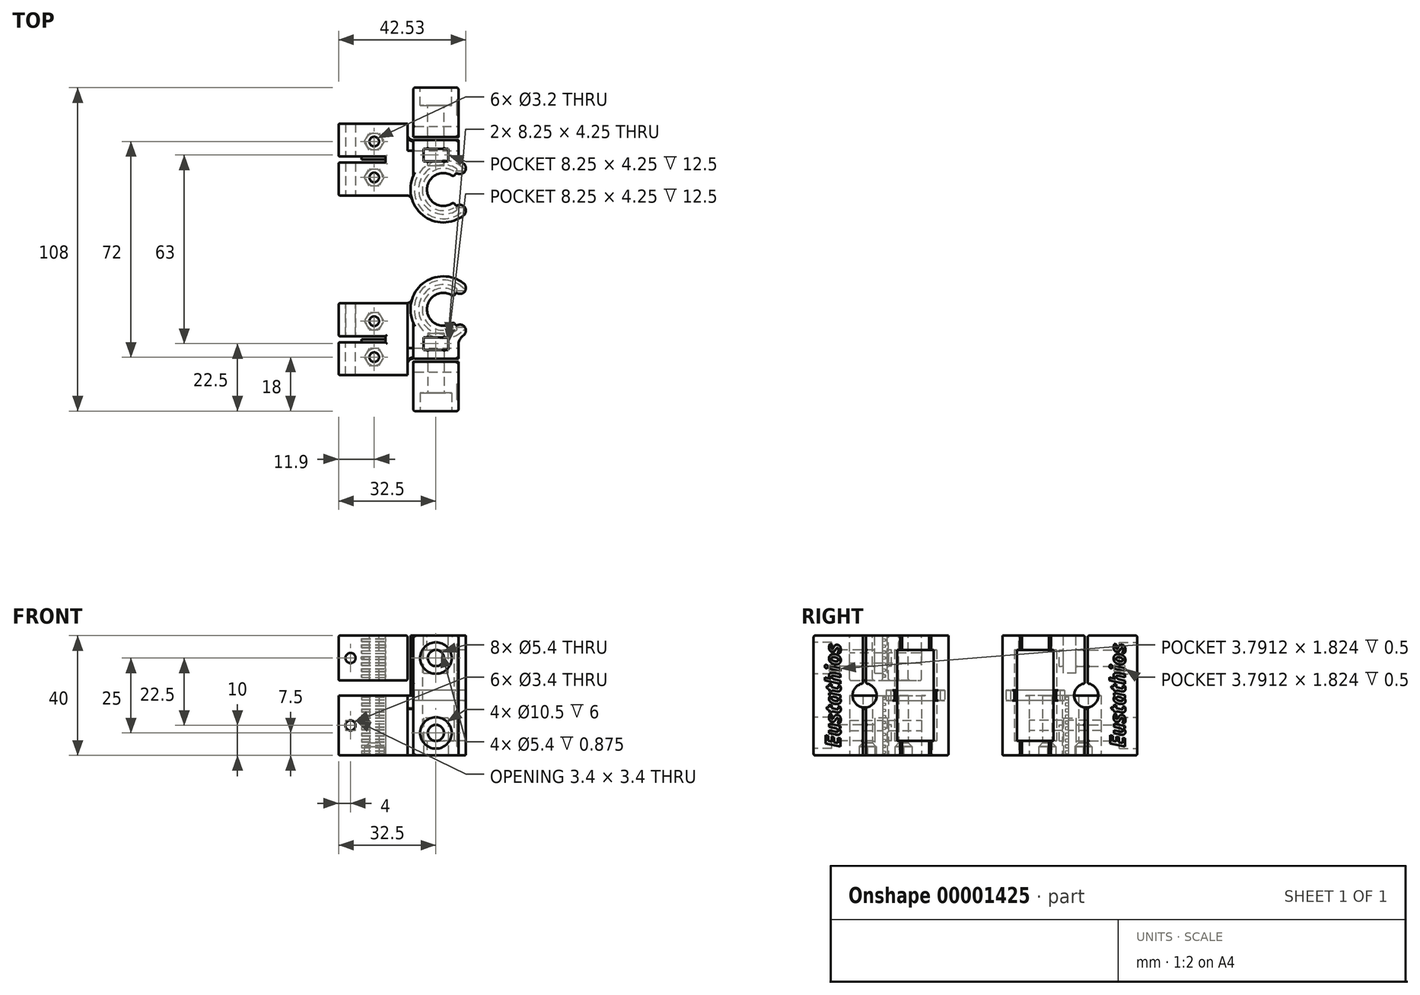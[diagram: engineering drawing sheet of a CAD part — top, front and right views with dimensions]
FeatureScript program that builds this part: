
annotation { "Feature Type Name" : "Feature", "Feature Type Description" : "" }
export const myFeature = defineFeature(function(context is Context, id is Id, definition is map)
    precondition{}
    {
        {
            var Q0;
            Q0=qCreatedBy(makeId("Top.planeOp"),FACE);
            var sketch = newSketch(context, id + "F0", { "sketchPlane" : qUnion([Q0])});
            skArc(sketch, "E0", {"start": v(5, -9.8) * mm, "mid": v(3.61, 10.39) * mm, "end": v(-10, -4.58) * mm});
            skLineSegment(sketch, "E1", {"start": v(5, -34) * mm, "end": v(5, -9.8) * mm});
            skLineSegment(sketch, "E2", {"start": v(-10, -4.58) * mm, "end": v(-10, -34) * mm});
            skLineSegment(sketch, "E3", {"start": v(-10, -34) * mm, "end": v(5, -34) * mm});
            skLineSegment(sketch, "E4", {"start": v(-10, -17) * mm, "end": v(5, -17) * mm, "construction": true});
            skSolve(sketch);
        }
        {
            var Q0;
            Q0=qSketchRegion(id+"F0",true);
            extrude(context, id + "F1", {"entities" : qUnion([Q0]), "depth" : 40 * mm});
        }
        {
            var Q0;
            Q0=makeQuery(id+"F1.opExtrude","CAP_FACE",FACE,{"disambiguationData":[OSD([sQuery(id+"F0.wireOp",EDGE,"E0"),sQuery(id+"F0.wireOp",EDGE,"E1"),sQuery(id+"F0.wireOp",EDGE,"E2"),sQuery(id+"F0.wireOp",EDGE,"E3")])],"isStart":true});
            var Q1;
            Q1=makeQuery(id+"F1.opExtrude","CAP_FACE",FACE,{"disambiguationData":[OSD([sQuery(id+"F0.wireOp",EDGE,"E0"),sQuery(id+"F0.wireOp",EDGE,"E1"),sQuery(id+"F0.wireOp",EDGE,"E2"),sQuery(id+"F0.wireOp",EDGE,"E3")])],"isStart":false});
            cPlane(context, id + "F2", {"entities" : qUnion([Q0, Q1]), "cplaneType" : CPlaneType.MID_PLANE, "offset" : 150 * mm, "width" : 150 * mm, "height" : 150 * mm});
        }
        {
            var Q0;
            Q0=makeQuery(id+"F1.opExtrude","CAP_FACE",FACE,{"disambiguationData":[OSD([sQuery(id+"F0.wireOp",EDGE,"E0"),sQuery(id+"F0.wireOp",EDGE,"E1"),sQuery(id+"F0.wireOp",EDGE,"E2"),sQuery(id+"F0.wireOp",EDGE,"E3")])],"isStart":true});
            var sketch = newSketch(context, id + "F3", { "sketchPlane" : qUnion([Q0])});
            skLineSegment(sketch, "E5", {"start": v(-35, -2) * mm, "end": v(-35, 9) * mm});
            skLineSegment(sketch, "E6", {"start": v(-35, 9) * mm, "end": v(-19.3, 9) * mm});
            skLineSegment(sketch, "E7", {"start": v(-19.3, 9) * mm, "end": v(-19.3, 11) * mm});
            skLineSegment(sketch, "E8", {"start": v(-19.3, 11) * mm, "end": v(-35, 11) * mm});
            skLineSegment(sketch, "E9", {"start": v(-35, 11) * mm, "end": v(-35, 22) * mm});
            skLineSegment(sketch, "E10", {"start": v(-35, 22) * mm, "end": v(-10, 22) * mm});
            skLineSegment(sketch, "E11", {"start": v(-10, 22) * mm, "end": v(-10, 4.58) * mm});
            skLineSegment(sketch, "E12", {"start": v(-35, 11) * mm, "end": v(-35, 9) * mm, "construction": true});
            skLineSegment(sketch, "E13", {"start": v(-35, 10) * mm, "end": v(-19.3, 10) * mm, "construction": true});
            skLineSegment(sketch, "E14", {"start": v(-35, -2) * mm, "end": v(-12.37, -2) * mm});
            skArc(sketch, "E15.0", {"start": v(-10.47, -3.38) * mm, "mid": v(-10.98, 0.64) * mm, "end": v(-10, 4.58) * mm});
            skArc(sketch, "E16", {"start": v(-12.37, -2) * mm, "mid": v(-11.2, -2.38) * mm, "end": v(-10.47, -3.38) * mm});
            skPoint(sketch, "E17.orphan", {"position": v(5, 9.8) * mm});
            skSolve(sketch);
        }
        {
            var Q0;
            Q0=qSketchRegion(id+"F3",true);
            var Q1;
            Q1=qCreatedBy(id+"F2.planeOp",FACE);
            extrude(context, id + "F4", {"entities" : qUnion([Q0]), "operationType" : NewBodyOperationType.ADD, "endBound" : BoundingType.UP_TO_SURFACE, "oppositeDirection" : true, "endBoundEntityFace" : qUnion([Q1]), "depth" : 21 * mm});
        }
        {
            var Q0;
            Q0=makeQuery(id+"F1.opExtrude","SWEPT_FACE",FACE,{"disambiguationData":[OSD([sQuery(id+"F0.wireOp",EDGE,"E1")])]});
            var sketch = newSketch(context, id + "F5", { "sketchPlane" : qUnion([Q0])});
            skLineSegment(sketch, "E18", {"start": v(0, 0) * mm, "end": v(0, 40) * mm, "construction": true});
            skLineSegment(sketch, "E19.0", {"start": v(-9.8, 40) * mm, "end": v(11, 40) * mm, "construction": true});
            skLineSegment(sketch, "E20", {"start": v(0, 20) * mm, "end": v(-17, 20) * mm, "construction": true});
            skPoint(sketch, "E20.endSnap0", {"position": v(0, 20) * mm});
            skLineSegment(sketch, "E21", {"start": v(-17, 20) * mm, "end": v(-34, 20) * mm, "construction": true});
            skCircle(sketch, "E22", {"center": v(-17, 20) * mm, "radius": 4.03 * mm});
            skSolve(sketch);
        }
        {
            var Q0;
            Q0=qSketchRegion(id+"F5",true);
            var Q1;
            Q1=makeQuery(id+"F1.opExtrude","SWEPT_FACE",FACE,{"disambiguationData":[OSD([sQuery(id+"F0.wireOp",EDGE,"E2")])]});
            extrude(context, id + "F6", {"entities" : qUnion([Q0]), "operationType" : NewBodyOperationType.REMOVE, "oppositeDirection" : true, "endBoundEntityFace" : qUnion([Q1]), "depth" : 17 * mm});
        }
        {
            var Q0;
            Q0=makeQuery(id+"F4.boolean.opBoolean","MERGE",FACE,{"derivedFrom":[makeQuery(id+"F1.opExtrude","CAP_FACE",FACE,{"disambiguationData":[OSD([sQuery(id+"F0.wireOp",EDGE,"E0"),sQuery(id+"F0.wireOp",EDGE,"E1"),sQuery(id+"F0.wireOp",EDGE,"E2"),sQuery(id+"F0.wireOp",EDGE,"E3")])],"isStart":true}),makeQuery(id+"F4.opExtrude","CAP_FACE",FACE,{"disambiguationData":[OSD([sQuery(id+"F3.wireOp",EDGE,"E5"),sQuery(id+"F3.wireOp",EDGE,"E6"),sQuery(id+"F3.wireOp",EDGE,"E7"),sQuery(id+"F3.wireOp",EDGE,"E8"),sQuery(id+"F3.wireOp",EDGE,"E9"),sQuery(id+"F3.wireOp",EDGE,"E10"),sQuery(id+"F3.wireOp",EDGE,"E11"),sQuery(id+"F3.wireOp",EDGE,"bca63a35-03c2-4865-813d-011e51dad5aa"),sQuery(id+"F3.wireOp",EDGE,"E14"),sQuery(id+"F3.wireOp",EDGE,"5d72e0aa-44b3-420c-8565-5770b2da08a5")])],"isStart":true})]});
            var sketch = newSketch(context, id + "F7", { "sketchPlane" : qUnion([Q0])});
            skLineSegment(sketch, "E23.0", {"start": v(-12, 12.98) * mm, "end": v(-10, 12.98) * mm, "construction": true});
            skLineSegment(sketch, "E24.0", {"start": v(-12, 12.97) * mm, "end": v(-12, 12.97) * mm});
            skLineSegment(sketch, "E25", {"start": v(-10, 17.5) * mm, "end": v(5, 17.5) * mm});
            skLineSegment(sketch, "E26", {"start": v(5, 17.5) * mm, "end": v(5, 16.5) * mm});
            skLineSegment(sketch, "E27", {"start": v(5, 17) * mm, "end": v(-12, 17) * mm, "construction": true});
            skLineSegment(sketch, "E28", {"start": v(5, 16.5) * mm, "end": v(-10, 16.5) * mm});
            skLineSegment(sketch, "E29.0", {"start": v(-12, 12.97) * mm, "end": v(-12, 21.03) * mm, "construction": true});
            skLineSegment(sketch, "E30", {"start": v(-10, 22) * mm, "end": v(-10, 17.5) * mm});
            skLineSegment(sketch, "E31", {"start": v(-10, 22) * mm, "end": v(-12, 22) * mm});
            skLineSegment(sketch, "E32", {"start": v(-12, 22) * mm, "end": v(-12, 18.5) * mm});
            skPoint(sketch, "E33.visualSharp", {"position": v(-12, 16.5) * mm});
            skArc(sketch, "E33.filletArc", {"start": v(-12, 18.5) * mm, "mid": v(-11.41, 17.09) * mm, "end": v(-10, 16.5) * mm});
            skSolve(sketch);
        }
        {
            var Q0;
            Q0=qSketchRegion(id+"F7",true);
            extrude(context, id + "F8", {"entities" : qUnion([Q0]), "operationType" : NewBodyOperationType.REMOVE, "endBound" : BoundingType.THROUGH_ALL, "oppositeDirection" : true, "depth" : 25 * mm});
        }
        {
            var Q0;
            {var subQ0=sQuery(id+"F3.wireOp",EDGE,"E10");var subQ1=sQuery(id+"F3.wireOp",EDGE,"E9");var subQ2=sQuery(id+"F3.wireOp",EDGE,"E8");var subQ3=sQuery(id+"F3.wireOp",EDGE,"E7");var subQ4=sQuery(id+"F0.wireOp",EDGE,"E1");var subQ5=sQuery(id+"F0.wireOp",EDGE,"E0");var subQ6=sQuery(id+"F3.wireOp",EDGE,"5d72e0aa-44b3-420c-8565-5770b2da08a5");var subQ7=sQuery(id+"F3.wireOp",EDGE,"E14");var subQ8=sQuery(id+"F3.wireOp",EDGE,"E5");var subQ9=sQuery(id+"F3.wireOp",EDGE,"E6");Q0=makeQuery(id+"F8.boolean.opBoolean","SPLIT",FACE,{"disambiguationData":[TD([makeQuery(id+"F1.opExtrude","SWEPT_FACE",FACE,{"disambiguationData":[OSD([subQ5])]})])],"derivedFrom":makeQuery(id+"F4.boolean.opBoolean","MERGE",FACE,{"derivedFrom":[makeQuery(id+"F1.opExtrude","CAP_FACE",FACE,{"disambiguationData":[OSD([subQ5,subQ4,sQuery(id+"F0.wireOp",EDGE,"E2"),sQuery(id+"F0.wireOp",EDGE,"E3")])],"isStart":true}),makeQuery(id+"F4.opExtrude","CAP_FACE",FACE,{"disambiguationData":[OSD([subQ8,subQ9,subQ3,subQ2,subQ1,subQ0,sQuery(id+"F3.wireOp",EDGE,"E11"),sQuery(id+"F3.wireOp",EDGE,"bca63a35-03c2-4865-813d-011e51dad5aa"),subQ7,subQ6])],"isStart":true})]})});}
            var sketch = newSketch(context, id + "F9", { "sketchPlane" : qUnion([Q0])});
            skCircle(sketch, "E34", {"center": v(0, 0) * mm, "radius": 7.05 * mm});
            skSolve(sketch);
        }
        {
            var Q0;
            Q0=qSketchRegion(id+"F9",true);
            extrude(context, id + "F10", {"entities" : qUnion([Q0]), "operationType" : NewBodyOperationType.REMOVE, "endBound" : BoundingType.THROUGH_ALL, "oppositeDirection" : true, "depth" : 25 * mm});
        }
        {
            var Q0;
            {var subQ0=sQuery(id+"F3.wireOp",EDGE,"E10");var subQ1=sQuery(id+"F3.wireOp",EDGE,"E9");var subQ2=sQuery(id+"F3.wireOp",EDGE,"E8");var subQ3=sQuery(id+"F3.wireOp",EDGE,"E7");var subQ4=sQuery(id+"F0.wireOp",EDGE,"E1");var subQ5=sQuery(id+"F0.wireOp",EDGE,"E0");var subQ6=sQuery(id+"F3.wireOp",EDGE,"5d72e0aa-44b3-420c-8565-5770b2da08a5");var subQ7=sQuery(id+"F3.wireOp",EDGE,"E14");var subQ8=sQuery(id+"F3.wireOp",EDGE,"E5");var subQ9=sQuery(id+"F3.wireOp",EDGE,"E6");Q0=makeQuery(id+"F8.boolean.opBoolean","SPLIT",FACE,{"disambiguationData":[TD([makeQuery(id+"F1.opExtrude","SWEPT_FACE",FACE,{"disambiguationData":[OSD([subQ5])]})])],"derivedFrom":makeQuery(id+"F4.boolean.opBoolean","MERGE",FACE,{"derivedFrom":[makeQuery(id+"F1.opExtrude","CAP_FACE",FACE,{"disambiguationData":[OSD([subQ5,subQ4,sQuery(id+"F0.wireOp",EDGE,"E2"),sQuery(id+"F0.wireOp",EDGE,"E3")])],"isStart":true}),makeQuery(id+"F4.opExtrude","CAP_FACE",FACE,{"disambiguationData":[OSD([subQ8,subQ9,subQ3,subQ2,subQ1,subQ0,sQuery(id+"F3.wireOp",EDGE,"E11"),sQuery(id+"F3.wireOp",EDGE,"bca63a35-03c2-4865-813d-011e51dad5aa"),subQ7,subQ6])],"isStart":true})]})});}
            var sketch = newSketch(context, id + "F11", { "sketchPlane" : qUnion([Q0])});
            skLineSegment(sketch, "E35", {"start": v(0, 0) * mm, "end": v(8.5, 6.98) * mm, "construction": true});
            skLineSegment(sketch, "E36", {"start": v(8.5, -6.98) * mm, "end": v(0, 0) * mm, "construction": true});
            skArc(sketch, "E37", {"start": v(6.77, -8.67) * mm, "mid": v(7.11, -5.9) * mm, "end": v(4.34, -5.56) * mm});
            skLineSegment(sketch, "E38", {"start": v(0, 0) * mm, "end": v(14.65, 0) * mm, "construction": true});
            skArc(sketch, "E39", {"start": v(4.34, 5.56) * mm, "mid": v(7.11, 5.9) * mm, "end": v(6.77, 8.67) * mm});
            skLineSegment(sketch, "E40", {"start": v(5.56, 7.11) * mm, "end": v(0, 0) * mm, "construction": true});
            skLineSegment(sketch, "E41", {"start": v(0, 0) * mm, "end": v(5.56, -7.11) * mm, "construction": true});
            skArc(sketch, "E42", {"start": v(4.34, 5.56) * mm, "mid": v(7.05, 0) * mm, "end": v(4.34, -5.56) * mm});
            skSolve(sketch);
        }
        {
            var Q0;
            Q0=qSketchRegion(id+"F11",true);
            var Q1;
            {var subQ2=sQuery(id+"F11.wireOp",EDGE,"E37");Q1=makeQuery(id+"F11.imprint","IMPRINT",FACE,{"disambiguationData":[TD([[makeQuery(id+"F11.imprint","IMPRINT",EDGE,{"derivedFrom":subQ2}),-1.0]])]});}
            extrude(context, id + "F12", {"entities" : qUnion([Q0, Q1]), "operationType" : NewBodyOperationType.REMOVE, "endBound" : BoundingType.THROUGH_ALL, "oppositeDirection" : true, "depth" : 25 * mm});
        }
        {
            var Q0;
            Q0=makeQuery(id+"F1.opExtrude","SWEPT_EDGE",EDGE,{"disambiguationData":[OSD([sQuery(id+"F0.wireOp",EDGE,"E0"),sQuery(id+"F0.wireOp",EDGE,"E1")])]});
            fillet(context, id + "F13", {"entities" : qUnion([Q0]), "radius" : 4 * mm, "tangentPropagation" : true, "allowEdgeOverflow" : false});
        }
        {
            var Q0;
            Q0=qCreatedBy(makeId("Right.planeOp"),FACE);
            var sketch = newSketch(context, id + "F14", { "sketchPlane" : qUnion([Q0])});
            skLineSegment(sketch, "E43.rect.bottom", {"start": v(-6.1, 35.2) * mm, "end": v(6.1, 35.2) * mm});
            skLineSegment(sketch, "E43.rect.top", {"start": v(-6.1, 4.8) * mm, "end": v(6.1, 4.8) * mm});
            skLineSegment(sketch, "E43.rect.left", {"start": v(-6.1, 35.2) * mm, "end": v(-6.1, 4.8) * mm});
            skLineSegment(sketch, "E43.rect.right", {"start": v(6.1, 35.2) * mm, "end": v(6.1, 4.8) * mm});
            skPoint(sketch, "E43.rect.middle", {"position": v(0, 20) * mm});
            skLineSegment(sketch, "E44", {"start": v(-5.14, 40) * mm, "end": v(-5.14, 0) * mm, "construction": true});
            skLineSegment(sketch, "E45", {"start": v(5.14, 0) * mm, "end": v(5.14, 40) * mm, "construction": true});
            skLineSegment(sketch, "E46", {"start": v(-5.14, 0) * mm, "end": v(5.14, 0) * mm, "construction": true});
            skLineSegment(sketch, "E47", {"start": v(-5.14, 40) * mm, "end": v(5.14, 40) * mm, "construction": true});
            skLineSegment(sketch, "E48", {"start": v(0, 0) * mm, "end": v(0, 40) * mm, "construction": true});
            skSolve(sketch);
        }
        {
            var Q0;
            Q0=qSketchRegion(id+"F14",true);
            extrude(context, id + "F15", {"entities" : qUnion([Q0]), "operationType" : NewBodyOperationType.REMOVE, "endBound" : BoundingType.THROUGH_ALL, "depth" : 25 * mm});
        }
        {
            var Q0;
            {var subQ0=sQuery(id+"F3.wireOp",EDGE,"E10");var subQ1=sQuery(id+"F3.wireOp",EDGE,"E9");var subQ2=sQuery(id+"F3.wireOp",EDGE,"E8");var subQ3=sQuery(id+"F3.wireOp",EDGE,"E7");var subQ4=sQuery(id+"F0.wireOp",EDGE,"E1");var subQ5=sQuery(id+"F0.wireOp",EDGE,"E0");var subQ6=sQuery(id+"F3.wireOp",EDGE,"5d72e0aa-44b3-420c-8565-5770b2da08a5");var subQ7=sQuery(id+"F3.wireOp",EDGE,"E14");var subQ8=sQuery(id+"F3.wireOp",EDGE,"E5");var subQ9=sQuery(id+"F3.wireOp",EDGE,"E6");Q0=makeQuery(id+"F8.boolean.opBoolean","SPLIT",FACE,{"disambiguationData":[TD([makeQuery(id+"F1.opExtrude","SWEPT_FACE",FACE,{"disambiguationData":[OSD([subQ5])]})])],"derivedFrom":makeQuery(id+"F4.boolean.opBoolean","MERGE",FACE,{"derivedFrom":[makeQuery(id+"F1.opExtrude","CAP_FACE",FACE,{"disambiguationData":[OSD([subQ5,subQ4,sQuery(id+"F0.wireOp",EDGE,"E2"),sQuery(id+"F0.wireOp",EDGE,"E3")])],"isStart":true}),makeQuery(id+"F4.opExtrude","CAP_FACE",FACE,{"disambiguationData":[OSD([subQ8,subQ9,subQ3,subQ2,subQ1,subQ0,sQuery(id+"F3.wireOp",EDGE,"E11"),sQuery(id+"F3.wireOp",EDGE,"bca63a35-03c2-4865-813d-011e51dad5aa"),subQ7,subQ6])],"isStart":true})]})});}
            var sketch = newSketch(context, id + "F16", { "sketchPlane" : qUnion([Q0])});
            skArc(sketch, "E49", {"start": v(3.39, 4.33) * mm, "mid": v(-5.5, 0) * mm, "end": v(3.39, -4.33) * mm});
            skArc(sketch, "E50.0", {"start": v(4.34, 5.56) * mm, "mid": v(-7.05, 0) * mm, "end": v(4.34, -5.56) * mm});
            skLineSegment(sketch, "E51", {"start": v(0, 0) * mm, "end": v(6.8, 5.58) * mm, "construction": true});
            skLineSegment(sketch, "E52", {"start": v(0, 0) * mm, "end": v(6.8, -5.58) * mm, "construction": true});
            skArc(sketch, "E53", {"start": v(4.34, 5.56) * mm, "mid": v(5.58, 5.14) * mm, "end": v(6.8, 5.58) * mm});
            skArc(sketch, "E54", {"start": v(4.34, -5.56) * mm, "mid": v(5.58, -5.14) * mm, "end": v(6.8, -5.58) * mm});
            skLineSegment(sketch, "E55", {"start": v(4.34, 5.56) * mm, "end": v(3.39, 4.33) * mm});
            skLineSegment(sketch, "E56", {"start": v(3.39, -4.33) * mm, "end": v(4.34, -5.56) * mm});
            skLineSegment(sketch, "E57", {"start": v(3.39, 4.33) * mm, "end": v(0, 0) * mm, "construction": true});
            skLineSegment(sketch, "E58", {"start": v(3.39, -4.33) * mm, "end": v(0, 0) * mm, "construction": true});
            skSolve(sketch);
        }
        {
            var Q0;
            Q0=qSketchRegion(id+"F16",true);
            var Q1;
            Q1=makeQuery(id+"F15.boolean.opBoolean","COPY",FACE,{"disambiguationData":[OD(0.0)],"derivedFrom":makeQuery(id+"F15.opExtrude","SWEPT_FACE",FACE,{"disambiguationData":[OSD([sQuery(id+"F14.wireOp",EDGE,"E43.rect.top")])]})});
            extrude(context, id + "F17", {"entities" : qUnion([Q0]), "operationType" : NewBodyOperationType.ADD, "endBound" : BoundingType.UP_TO_SURFACE, "oppositeDirection" : true, "endBoundEntityFace" : qUnion([Q1]), "depth" : 2.4 * mm});
        }
        {
            var Q0;
            {var subQ0=sQuery(id+"F0.wireOp",EDGE,"E0");var subQ1=sQuery(id+"F0.wireOp",EDGE,"E1");var subQ2=sQuery(id+"F0.wireOp",EDGE,"E2");Q0=makeQuery(id+"F8.boolean.opBoolean","SPLIT",FACE,{"disambiguationData":[TD([makeQuery(id+"F1.opExtrude","SWEPT_FACE",FACE,{"disambiguationData":[OSD([subQ0])]})])],"derivedFrom":makeQuery(id+"F1.opExtrude","CAP_FACE",FACE,{"disambiguationData":[OSD([subQ0,subQ1,subQ2,sQuery(id+"F0.wireOp",EDGE,"E3")])],"isStart":false})});}
            var sketch = newSketch(context, id + "F18", { "sketchPlane" : qUnion([Q0])});
            skArc(sketch, "E59.0", {"start": v(3.39, -4.33) * mm, "mid": v(-5.5, 0) * mm, "end": v(3.39, 4.33) * mm});
            skLineSegment(sketch, "E60.0", {"start": v(4.34, -5.56) * mm, "end": v(3.39, -4.33) * mm});
            skLineSegment(sketch, "E61.0", {"start": v(3.39, 4.33) * mm, "end": v(4.34, 5.56) * mm});
            skArc(sketch, "E62.0", {"start": v(4.34, 5.56) * mm, "mid": v(-7.05, 0) * mm, "end": v(4.34, -5.56) * mm});
            skSolve(sketch);
        }
        {
            var Q0;
            Q0=qSketchRegion(id+"F18",true);
            var Q1;
            Q1=makeQuery(id+"F15.boolean.opBoolean","COPY",FACE,{"disambiguationData":[OD(0.0)],"derivedFrom":makeQuery(id+"F15.opExtrude","SWEPT_FACE",FACE,{"disambiguationData":[OSD([sQuery(id+"F14.wireOp",EDGE,"E43.rect.bottom")])]})});
            extrude(context, id + "F19", {"entities" : qUnion([Q0]), "operationType" : NewBodyOperationType.ADD, "endBound" : BoundingType.UP_TO_SURFACE, "oppositeDirection" : true, "endBoundEntityFace" : qUnion([Q1]), "depth" : 2.4 * mm});
        }
        {
            var Q0;
            {var subQ0=sQuery(id+"F0.wireOp",EDGE,"E0");var subQ1=sQuery(id+"F0.wireOp",EDGE,"E1");var subQ2=sQuery(id+"F0.wireOp",EDGE,"E2");Q0=makeQuery(id+"F19.boolean.opBoolean","MERGE",FACE,{"derivedFrom":[makeQuery(id+"F8.boolean.opBoolean","SPLIT",FACE,{"disambiguationData":[TD([makeQuery(id+"F1.opExtrude","SWEPT_FACE",FACE,{"disambiguationData":[OSD([subQ0])]})])],"derivedFrom":makeQuery(id+"F1.opExtrude","CAP_FACE",FACE,{"disambiguationData":[OSD([subQ0,subQ1,subQ2,sQuery(id+"F0.wireOp",EDGE,"E3")])],"isStart":false})}),makeQuery(id+"F19.opExtrude","CAP_FACE",FACE,{"disambiguationData":[OSD([sQuery(id+"F18.wireOp",EDGE,"825981b6-10bd-436c-b23c-b1dcfb23399f.0"),sQuery(id+"F18.wireOp",EDGE,"26848335-8289-480a-91f7-f3094b967ab5.0"),sQuery(id+"F18.wireOp",EDGE,"958e6e3c-ce8c-4eca-b8df-495d4845233b.0"),sQuery(id+"F18.wireOp",EDGE,"a21f0ce2-bef5-4404-b2f3-7f19712db0ed.0"),sQuery(id+"F18.wireOp",EDGE,"5b232a10-1d2d-4218-a2a3-206db68530f9.0"),sQuery(id+"F18.wireOp",EDGE,"9355f6d4-eb2a-417f-8d43-74a68f565168.0")])],"isStart":true})]});}
            var sketch = newSketch(context, id + "F20", { "sketchPlane" : qUnion([Q0])});
            skLineSegment(sketch, "E63", {"start": v(-2.5, -16.5) * mm, "end": v(-2.5, -11.5) * mm, "construction": true});
            skLineSegment(sketch, "E64.rect.bottom", {"start": v(-6.62, -13.62) * mm, "end": v(1.63, -13.62) * mm});
            skLineSegment(sketch, "E64.rect.top", {"start": v(-6.62, -9.38) * mm, "end": v(1.63, -9.38) * mm});
            skLineSegment(sketch, "E64.rect.left", {"start": v(-6.62, -13.62) * mm, "end": v(-6.62, -9.38) * mm});
            skLineSegment(sketch, "E64.rect.right", {"start": v(1.63, -13.63) * mm, "end": v(1.63, -9.38) * mm});
            skPoint(sketch, "E64.rect.middle", {"position": v(-2.5, -11.5) * mm});
            skSolve(sketch);
        }
        {
            var Q0;
            Q0=qSketchRegion(id+"F20",true);
            extrude(context, id + "F21", {"entities" : qUnion([Q0]), "operationType" : NewBodyOperationType.REMOVE, "oppositeDirection" : true, "depth" : 12.5 * mm});
        }
        {
            var Q0;
            {var subQ0=sQuery(id+"F3.wireOp",EDGE,"E10");var subQ1=sQuery(id+"F3.wireOp",EDGE,"E9");var subQ2=sQuery(id+"F3.wireOp",EDGE,"E8");var subQ3=sQuery(id+"F3.wireOp",EDGE,"E7");var subQ4=sQuery(id+"F0.wireOp",EDGE,"E1");var subQ5=sQuery(id+"F0.wireOp",EDGE,"E0");var subQ6=sQuery(id+"F3.wireOp",EDGE,"5d72e0aa-44b3-420c-8565-5770b2da08a5");var subQ7=sQuery(id+"F3.wireOp",EDGE,"E14");var subQ8=sQuery(id+"F3.wireOp",EDGE,"E5");var subQ9=sQuery(id+"F3.wireOp",EDGE,"E6");Q0=makeQuery(id+"F17.boolean.opBoolean","MERGE",FACE,{"derivedFrom":[makeQuery(id+"F8.boolean.opBoolean","SPLIT",FACE,{"disambiguationData":[TD([makeQuery(id+"F1.opExtrude","SWEPT_FACE",FACE,{"disambiguationData":[OSD([subQ5])]})])],"derivedFrom":makeQuery(id+"F4.boolean.opBoolean","MERGE",FACE,{"derivedFrom":[makeQuery(id+"F1.opExtrude","CAP_FACE",FACE,{"disambiguationData":[OSD([subQ5,subQ4,sQuery(id+"F0.wireOp",EDGE,"E2"),sQuery(id+"F0.wireOp",EDGE,"E3")])],"isStart":true}),makeQuery(id+"F4.opExtrude","CAP_FACE",FACE,{"disambiguationData":[OSD([subQ8,subQ9,subQ3,subQ2,subQ1,subQ0,sQuery(id+"F3.wireOp",EDGE,"E11"),sQuery(id+"F3.wireOp",EDGE,"bca63a35-03c2-4865-813d-011e51dad5aa"),subQ7,subQ6])],"isStart":true})]})}),makeQuery(id+"F17.opExtrude","CAP_FACE",FACE,{"disambiguationData":[OSD([sQuery(id+"F16.wireOp",EDGE,"E49"),sQuery(id+"F16.wireOp",EDGE,"E50.0"),sQuery(id+"F16.wireOp",EDGE,"E55"),sQuery(id+"F16.wireOp",EDGE,"E56")])],"isStart":true})]});}
            var sketch = newSketch(context, id + "F22", { "sketchPlane" : qUnion([Q0])});
            skLineSegment(sketch, "E65.0.0", {"start": v(-6.62, 9.38) * mm, "end": v(-6.62, 13.62) * mm});
            skLineSegment(sketch, "E65.0.1", {"start": v(-6.62, 13.62) * mm, "end": v(1.63, 13.62) * mm});
            skLineSegment(sketch, "E65.0.2", {"start": v(1.63, 13.62) * mm, "end": v(1.63, 9.38) * mm});
            skLineSegment(sketch, "E65.0.3", {"start": v(1.63, 9.38) * mm, "end": v(-6.62, 9.38) * mm});
            skSolve(sketch);
        }
        {
            var Q0;
            Q0=qSketchRegion(id+"F22",true);
            extrude(context, id + "F23", {"entities" : qUnion([Q0]), "operationType" : NewBodyOperationType.REMOVE, "oppositeDirection" : true, "depth" : 12.5 * mm});
        }
        {
            var Q0;
            Q0=makeQuery(id+"F1.opExtrude","SWEPT_FACE",FACE,{"disambiguationData":[OSD([sQuery(id+"F0.wireOp",EDGE,"E3")])]});
            var sketch = newSketch(context, id + "F24", { "sketchPlane" : qUnion([Q0])});
            skLineSegment(sketch, "E66", {"start": v(-2.5, 0) * mm, "end": v(-2.5, 7.5) * mm, "construction": true});
            skLineSegment(sketch, "E67", {"start": v(-2.5, 7.5) * mm, "end": v(-2.5, 32.5) * mm, "construction": true});
            skLineSegment(sketch, "E68", {"start": v(-2.5, 32.5) * mm, "end": v(-2.5, 40) * mm, "construction": true});
            skLineSegment(sketch, "E69", {"start": v(-2.5, 7.5) * mm, "end": v(-10, 7.5) * mm, "construction": true});
            skLineSegment(sketch, "E70", {"start": v(-2.5, 32.5) * mm, "end": v(-10, 32.5) * mm, "construction": true});
            skCircle(sketch, "E71", {"center": v(-2.5, 7.5) * mm, "radius": 2.7 * mm});
            skCircle(sketch, "E72", {"center": v(-2.5, 32.5) * mm, "radius": 2.7 * mm});
            skSolve(sketch);
        }
        {
            var Q0;
            Q0=qSketchRegion(id+"F24",true);
            extrude(context, id + "F25", {"entities" : qUnion([Q0]), "operationType" : NewBodyOperationType.REMOVE, "oppositeDirection" : true, "depth" : 26 * mm, "offsetDistance" : 25 * mm});
        }
        {
            var Q0;
            Q0=makeQuery(id+"F1.opExtrude","SWEPT_FACE",FACE,{"disambiguationData":[OSD([sQuery(id+"F0.wireOp",EDGE,"E3")])]});
            var sketch = newSketch(context, id + "F26", { "sketchPlane" : qUnion([Q0])});
            skCircle(sketch, "E73", {"center": v(-2.5, 32.5) * mm, "radius": 5.25 * mm});
            skCircle(sketch, "E74", {"center": v(-2.5, 7.5) * mm, "radius": 5.25 * mm});
            skSolve(sketch);
        }
        {
            var Q0;
            Q0=qSketchRegion(id+"F26",true);
            extrude(context, id + "F27", {"entities" : qUnion([Q0]), "operationType" : NewBodyOperationType.REMOVE, "oppositeDirection" : true, "depth" : 6 * mm});
        }
        {
            var Q0;
            Q0=makeQuery(id+"F8.boolean.opBoolean","INTERSECT",EDGE,{"derivedFrom":[makeQuery(id+"F6.boolean.opBoolean","COPY",FACE,{"derivedFrom":makeQuery(id+"F6.opExtrude","SWEPT_FACE",FACE,{"disambiguationData":[OSD([sQuery(id+"F5.wireOp",EDGE,"E22")])]})}),makeQuery(id+"F8.opExtrude","SWEPT_FACE",FACE,{"disambiguationData":[OSD([sQuery(id+"F7.wireOp",EDGE,"E30")])]})]});
            var Q1;
            Q1=makeQuery(id+"F8.boolean.opBoolean","INTERSECT",EDGE,{"disambiguationData":[OD(0.0)],"derivedFrom":[makeQuery(id+"F6.boolean.opBoolean","COPY",FACE,{"derivedFrom":makeQuery(id+"F6.opExtrude","SWEPT_FACE",FACE,{"disambiguationData":[OSD([sQuery(id+"F5.wireOp",EDGE,"E22")])]})}),makeQuery(id+"F8.opExtrude","SWEPT_FACE",FACE,{"disambiguationData":[OSD([sQuery(id+"F7.wireOp",EDGE,"E25")])]})]});
            var Q2;
            Q2=makeQuery(id+"F8.boolean.opBoolean","INTERSECT",EDGE,{"disambiguationData":[OD(1.0)],"derivedFrom":[makeQuery(id+"F6.boolean.opBoolean","COPY",FACE,{"derivedFrom":makeQuery(id+"F6.opExtrude","SWEPT_FACE",FACE,{"disambiguationData":[OSD([sQuery(id+"F5.wireOp",EDGE,"E22")])]})}),makeQuery(id+"F8.opExtrude","SWEPT_FACE",FACE,{"disambiguationData":[OSD([sQuery(id+"F7.wireOp",EDGE,"E25")])]})]});
            var Q3;
            Q3=makeQuery(id+"F8.boolean.opBoolean","COPY",EDGE,{"disambiguationData":[OD(0.0)],"derivedFrom":makeQuery(id+"F8.opExtrude","SWEPT_EDGE",EDGE,{"disambiguationData":[OSD([sQuery(id+"F7.wireOp",EDGE,"E25"),sQuery(id+"F7.wireOp",EDGE,"E30")])]})});
            var Q4;
            Q4=makeQuery(id+"F8.boolean.opBoolean","COPY",EDGE,{"disambiguationData":[OD(1.0)],"derivedFrom":makeQuery(id+"F8.opExtrude","SWEPT_EDGE",EDGE,{"disambiguationData":[OSD([sQuery(id+"F7.wireOp",EDGE,"E25"),sQuery(id+"F7.wireOp",EDGE,"E30")])]})});
            var Q5;
            Q5=makeQuery(id+"F8.boolean.opBoolean","INTERSECT",EDGE,{"derivedFrom":[makeQuery(id+"F1.opExtrude","CAP_FACE",FACE,{"disambiguationData":[OSD([sQuery(id+"F0.wireOp",EDGE,"E0"),sQuery(id+"F0.wireOp",EDGE,"E1"),sQuery(id+"F0.wireOp",EDGE,"E2"),sQuery(id+"F0.wireOp",EDGE,"E3")])],"isStart":false}),makeQuery(id+"F8.opExtrude","SWEPT_FACE",FACE,{"disambiguationData":[OSD([sQuery(id+"F7.wireOp",EDGE,"E25")])]})]});
            var Q6;
            {var subQ0=sQuery(id+"F0.wireOp",EDGE,"E2");var subQ1=sQuery(id+"F0.wireOp",EDGE,"E3");Q6=makeQuery(id+"F8.boolean.opBoolean","SPLIT",EDGE,{"disambiguationData":[TD([makeQuery(id+"F1.opExtrude","SWEPT_FACE",FACE,{"disambiguationData":[OSD([subQ1])]})])],"derivedFrom":makeQuery(id+"F1.opExtrude","CAP_EDGE",EDGE,{"disambiguationData":[OSD([subQ0])],"isStart":false})});}
            var Q7;
            Q7=makeQuery(id+"F1.opExtrude","CAP_EDGE",EDGE,{"disambiguationData":[OSD([sQuery(id+"F0.wireOp",EDGE,"E3")])],"isStart":false});
            var Q8;
            {var subQ0=sQuery(id+"F0.wireOp",EDGE,"E1");var subQ1=sQuery(id+"F0.wireOp",EDGE,"E3");Q8=makeQuery(id+"F8.boolean.opBoolean","SPLIT",EDGE,{"disambiguationData":[TD([makeQuery(id+"F1.opExtrude","SWEPT_FACE",FACE,{"disambiguationData":[OSD([subQ1])]})])],"derivedFrom":makeQuery(id+"F1.opExtrude","CAP_EDGE",EDGE,{"disambiguationData":[OSD([subQ0])],"isStart":false})});}
            var Q9;
            Q9=makeQuery(id+"F1.opExtrude","SWEPT_EDGE",EDGE,{"disambiguationData":[OSD([sQuery(id+"F0.wireOp",EDGE,"E2"),sQuery(id+"F0.wireOp",EDGE,"E3")])]});
            var Q10;
            Q10=makeQuery(id+"F1.opExtrude","SWEPT_EDGE",EDGE,{"disambiguationData":[OSD([sQuery(id+"F0.wireOp",EDGE,"E1"),sQuery(id+"F0.wireOp",EDGE,"E3")])]});
            var Q11;
            Q11=makeQuery(id+"F1.opExtrude","CAP_EDGE",EDGE,{"disambiguationData":[OSD([sQuery(id+"F0.wireOp",EDGE,"E3")])],"isStart":true});
            var Q12;
            Q12=makeQuery(id+"F8.boolean.opBoolean","COPY",EDGE,{"disambiguationData":[OD(1.0)],"derivedFrom":makeQuery(id+"F8.opExtrude","SWEPT_EDGE",EDGE,{"disambiguationData":[OSD([sQuery(id+"F0.wireOp",EDGE,"E1"),sQuery(id+"F7.wireOp",EDGE,"E25"),sQuery(id+"F7.wireOp",EDGE,"E26")])]})});
            var Q13;
            Q13=makeQuery(id+"F8.boolean.opBoolean","INTERSECT",EDGE,{"disambiguationData":[OD(1.0)],"derivedFrom":[makeQuery(id+"F6.boolean.opBoolean","COPY",FACE,{"derivedFrom":makeQuery(id+"F6.opExtrude","SWEPT_FACE",FACE,{"disambiguationData":[OSD([sQuery(id+"F5.wireOp",EDGE,"E22")])]})}),makeQuery(id+"F8.opExtrude","SWEPT_FACE",FACE,{"disambiguationData":[OSD([sQuery(id+"F7.wireOp",EDGE,"E25")])]})]});
            var Q14;
            Q14=makeQuery(id+"F8.boolean.opBoolean","COPY",EDGE,{"disambiguationData":[OD(0.0)],"derivedFrom":makeQuery(id+"F8.opExtrude","SWEPT_EDGE",EDGE,{"disambiguationData":[OSD([sQuery(id+"F0.wireOp",EDGE,"E1"),sQuery(id+"F7.wireOp",EDGE,"E25"),sQuery(id+"F7.wireOp",EDGE,"E26")])]})});
            var Q15;
            Q15=makeQuery(id+"F8.boolean.opBoolean","COPY",EDGE,{"derivedFrom":makeQuery(id+"F8.opExtrude","CAP_EDGE",EDGE,{"disambiguationData":[OSD([sQuery(id+"F7.wireOp",EDGE,"E25")])],"isStart":true})});
            var Q16;
            {var subQ0=sQuery(id+"F0.wireOp",EDGE,"E1");var subQ1=sQuery(id+"F0.wireOp",EDGE,"E3");Q16=makeQuery(id+"F8.boolean.opBoolean","SPLIT",EDGE,{"disambiguationData":[TD([makeQuery(id+"F1.opExtrude","SWEPT_FACE",FACE,{"disambiguationData":[OSD([subQ1])]})])],"derivedFrom":makeQuery(id+"F1.opExtrude","CAP_EDGE",EDGE,{"disambiguationData":[OSD([subQ0])],"isStart":true})});}
            var Q17;
            Q17=makeQuery(id+"F8.boolean.opBoolean","MERGE",EDGE,{"derivedFrom":[makeQuery(id+"F1.opExtrude","CAP_EDGE",EDGE,{"disambiguationData":[OSD([sQuery(id+"F0.wireOp",EDGE,"E2")])],"isStart":true}),makeQuery(id+"F8.opExtrude","CAP_EDGE",EDGE,{"disambiguationData":[OSD([sQuery(id+"F7.wireOp",EDGE,"E30")])],"isStart":true})]});
            var Q18;
            Q18=makeQuery(id+"F8.boolean.opBoolean","INTERSECT",EDGE,{"disambiguationData":[OD(0.0)],"derivedFrom":[makeQuery(id+"F6.boolean.opBoolean","COPY",FACE,{"derivedFrom":makeQuery(id+"F6.opExtrude","SWEPT_FACE",FACE,{"disambiguationData":[OSD([sQuery(id+"F5.wireOp",EDGE,"E22")])]})}),makeQuery(id+"F8.opExtrude","SWEPT_FACE",FACE,{"disambiguationData":[OSD([sQuery(id+"F7.wireOp",EDGE,"E25")])]})]});
            var Q19;
            {var subQ0=sQuery(id+"F5.wireOp",EDGE,"E22");Q19=makeQuery(id+"F8.boolean.opBoolean","SPLIT",EDGE,{"disambiguationData":[TD([makeQuery(id+"F8.opExtrude","SWEPT_FACE",FACE,{"disambiguationData":[OSD([sQuery(id+"F7.wireOp",EDGE,"E25")])]})])],"derivedFrom":makeQuery(id+"F6.boolean.opBoolean","COPY",EDGE,{"derivedFrom":makeQuery(id+"F6.opExtrude","CAP_EDGE",EDGE,{"disambiguationData":[OSD([subQ0])],"isStart":true})})});}
            var Q20;
            Q20=makeQuery(id+"F27.boolean.opBoolean","COPY",EDGE,{"derivedFrom":makeQuery(id+"F27.opExtrude","CAP_EDGE",EDGE,{"disambiguationData":[OSD([sQuery(id+"F26.wireOp",EDGE,"E74")])],"isStart":true})});
            var Q21;
            Q21=makeQuery(id+"F27.boolean.opBoolean","COPY",EDGE,{"derivedFrom":makeQuery(id+"F27.opExtrude","CAP_EDGE",EDGE,{"disambiguationData":[OSD([sQuery(id+"F26.wireOp",EDGE,"E73")])],"isStart":true})});
            var Q22;
            Q22=makeQuery(id+"F27.boolean.opBoolean","INTERSECT",EDGE,{"derivedFrom":[makeQuery(id+"F25.boolean.opBoolean","COPY",FACE,{"disambiguationData":[OD(0.0)],"derivedFrom":makeQuery(id+"F25.opExtrude","SWEPT_FACE",FACE,{"disambiguationData":[OSD([sQuery(id+"F24.wireOp",EDGE,"E71")])]})}),makeQuery(id+"F27.opExtrude","CAP_FACE",FACE,{"disambiguationData":[OSD([sQuery(id+"F26.wireOp",EDGE,"E74")])],"isStart":false})]});
            var Q23;
            Q23=makeQuery(id+"F27.boolean.opBoolean","INTERSECT",EDGE,{"derivedFrom":[makeQuery(id+"F25.boolean.opBoolean","COPY",FACE,{"disambiguationData":[OD(0.0)],"derivedFrom":makeQuery(id+"F25.opExtrude","SWEPT_FACE",FACE,{"disambiguationData":[OSD([sQuery(id+"F24.wireOp",EDGE,"E72")])]})}),makeQuery(id+"F27.opExtrude","CAP_FACE",FACE,{"disambiguationData":[OSD([sQuery(id+"F26.wireOp",EDGE,"E73")])],"isStart":false})]});
            var Q24;
            Q24=makeQuery(id+"F25.boolean.opBoolean","INTERSECT",EDGE,{"derivedFrom":[makeQuery(id+"F8.boolean.opBoolean","COPY",FACE,{"disambiguationData":[OD(1.0)],"derivedFrom":makeQuery(id+"F8.opExtrude","SWEPT_FACE",FACE,{"disambiguationData":[OSD([sQuery(id+"F7.wireOp",EDGE,"E25")])]})}),makeQuery(id+"F25.opExtrude","SWEPT_FACE",FACE,{"disambiguationData":[OSD([sQuery(id+"F24.wireOp",EDGE,"E72")])]})]});
            var Q25;
            Q25=makeQuery(id+"F25.boolean.opBoolean","INTERSECT",EDGE,{"derivedFrom":[makeQuery(id+"F8.boolean.opBoolean","COPY",FACE,{"disambiguationData":[OD(0.0)],"derivedFrom":makeQuery(id+"F8.opExtrude","SWEPT_FACE",FACE,{"disambiguationData":[OSD([sQuery(id+"F7.wireOp",EDGE,"E25")])]})}),makeQuery(id+"F25.opExtrude","SWEPT_FACE",FACE,{"disambiguationData":[OSD([sQuery(id+"F24.wireOp",EDGE,"E71")])]})]});
            fillet(context, id + "F28", {"entities" : qUnion([Q0, Q1, Q2, Q3, Q4, Q5, Q6, Q7, Q8, Q9, Q10, Q11, Q12, Q13, Q14, Q15, Q16, Q17, Q18, Q19, Q20, Q21, Q22, Q23, Q24, Q25]), "radius" : .5 * mm, "tangentPropagation" : true, "allowEdgeOverflow" : false});
        }
        {
            var Q0;
            {var subQ0=sQuery(id+"F3.wireOp",EDGE,"E10");var subQ1=sQuery(id+"F3.wireOp",EDGE,"E9");var subQ2=sQuery(id+"F3.wireOp",EDGE,"E8");var subQ3=sQuery(id+"F3.wireOp",EDGE,"E7");var subQ4=sQuery(id+"F0.wireOp",EDGE,"E1");var subQ5=sQuery(id+"F0.wireOp",EDGE,"E0");var subQ6=sQuery(id+"F3.wireOp",EDGE,"5d72e0aa-44b3-420c-8565-5770b2da08a5");var subQ7=sQuery(id+"F3.wireOp",EDGE,"E14");var subQ8=sQuery(id+"F3.wireOp",EDGE,"E5");var subQ9=sQuery(id+"F3.wireOp",EDGE,"E6");Q0=makeQuery(id+"F17.boolean.opBoolean","MERGE",FACE,{"derivedFrom":[makeQuery(id+"F8.boolean.opBoolean","SPLIT",FACE,{"disambiguationData":[TD([makeQuery(id+"F1.opExtrude","SWEPT_FACE",FACE,{"disambiguationData":[OSD([subQ5])]})])],"derivedFrom":makeQuery(id+"F4.boolean.opBoolean","MERGE",FACE,{"derivedFrom":[makeQuery(id+"F1.opExtrude","CAP_FACE",FACE,{"disambiguationData":[OSD([subQ5,subQ4,sQuery(id+"F0.wireOp",EDGE,"E2"),sQuery(id+"F0.wireOp",EDGE,"E3")])],"isStart":true}),makeQuery(id+"F4.opExtrude","CAP_FACE",FACE,{"disambiguationData":[OSD([subQ8,subQ9,subQ3,subQ2,subQ1,subQ0,sQuery(id+"F3.wireOp",EDGE,"E11"),sQuery(id+"F3.wireOp",EDGE,"bca63a35-03c2-4865-813d-011e51dad5aa"),subQ7,subQ6])],"isStart":true})]})}),makeQuery(id+"F17.opExtrude","CAP_FACE",FACE,{"disambiguationData":[OSD([sQuery(id+"F16.wireOp",EDGE,"E49"),sQuery(id+"F16.wireOp",EDGE,"E50.0"),sQuery(id+"F16.wireOp",EDGE,"E55"),sQuery(id+"F16.wireOp",EDGE,"E56")])],"isStart":true})]});}
            var sketch = newSketch(context, id + "F29", { "sketchPlane" : qUnion([Q0])});
            skLineSegment(sketch, "E75", {"start": v(-35, 11) * mm, "end": v(-35, 9) * mm, "construction": true});
            skLineSegment(sketch, "E76", {"start": v(-35, 10) * mm, "end": v(-23.1, 10) * mm, "construction": true});
            skLineSegment(sketch, "E77", {"start": v(-23.1, 16) * mm, "end": v(-23.1, 4) * mm, "construction": true});
            skCircle(sketch, "E78", {"center": v(-23.1, 16) * mm, "radius": 1.6 * mm});
            skCircle(sketch, "E79", {"center": v(-23.1, 4) * mm, "radius": 1.6 * mm});
            skSolve(sketch);
        }
        {
            var Q0;
            Q0=qSketchRegion(id+"F29",true);
            extrude(context, id + "F30", {"entities" : qUnion([Q0]), "operationType" : NewBodyOperationType.REMOVE, "endBound" : BoundingType.THROUGH_ALL, "oppositeDirection" : true, "depth" : 25 * mm});
        }
        {
            var Q0;
            Q0=makeQuery(id+"F4.opExtrude","SWEPT_FACE",FACE,{"disambiguationData":[OSD([sQuery(id+"F3.wireOp",EDGE,"E7")])]});
            var sketch = newSketch(context, id + "F31", { "sketchPlane" : qUnion([Q0])});
            skLineSegment(sketch, "E80", {"start": v(11, 19.5) * mm, "end": v(10, 19.4) * mm});
            skLineSegment(sketch, "E81", {"start": v(10, 19.4) * mm, "end": v(10, 18.6) * mm});
            skLineSegment(sketch, "E82", {"start": v(10, 18.6) * mm, "end": v(11, 18.5) * mm});
            skLineSegment(sketch, "E83", {"start": v(11, 18.5) * mm, "end": v(11, 19.5) * mm});
            skLineSegment(sketch, "E84.0.1.0", {"start": v(11, 17.5) * mm, "end": v(10, 17.4) * mm});
            skLineSegment(sketch, "E84.0.1.1", {"start": v(11, 16.5) * mm, "end": v(11, 17.5) * mm});
            skLineSegment(sketch, "E84.0.1.2", {"start": v(10, 16.6) * mm, "end": v(11, 16.5) * mm});
            skLineSegment(sketch, "E84.0.1.3", {"start": v(10, 17.4) * mm, "end": v(10, 16.6) * mm});
            skLineSegment(sketch, "E84.0.2.0", {"start": v(11, 15.5) * mm, "end": v(10, 15.4) * mm});
            skLineSegment(sketch, "E84.0.2.1", {"start": v(11, 14.5) * mm, "end": v(11, 15.5) * mm});
            skLineSegment(sketch, "E84.0.2.2", {"start": v(10, 14.6) * mm, "end": v(11, 14.5) * mm});
            skLineSegment(sketch, "E84.0.2.3", {"start": v(10, 15.4) * mm, "end": v(10, 14.6) * mm});
            skLineSegment(sketch, "E84.0.3.0", {"start": v(11, 13.5) * mm, "end": v(10, 13.4) * mm});
            skLineSegment(sketch, "E84.0.3.1", {"start": v(11, 12.5) * mm, "end": v(11, 13.5) * mm});
            skLineSegment(sketch, "E84.0.3.2", {"start": v(10, 12.6) * mm, "end": v(11, 12.5) * mm});
            skLineSegment(sketch, "E84.0.3.3", {"start": v(10, 13.4) * mm, "end": v(10, 12.6) * mm});
            skLineSegment(sketch, "E84.0.4.0", {"start": v(11, 11.5) * mm, "end": v(10, 11.4) * mm});
            skLineSegment(sketch, "E84.0.4.1", {"start": v(11, 10.5) * mm, "end": v(11, 11.5) * mm});
            skLineSegment(sketch, "E84.0.4.2", {"start": v(10, 10.6) * mm, "end": v(11, 10.5) * mm});
            skLineSegment(sketch, "E84.0.4.3", {"start": v(10, 11.4) * mm, "end": v(10, 10.6) * mm});
            skLineSegment(sketch, "E84.0.5.0", {"start": v(11, 9.5) * mm, "end": v(10, 9.4) * mm});
            skLineSegment(sketch, "E84.0.5.1", {"start": v(11, 8.5) * mm, "end": v(11, 9.5) * mm});
            skLineSegment(sketch, "E84.0.5.2", {"start": v(10, 8.6) * mm, "end": v(11, 8.5) * mm});
            skLineSegment(sketch, "E84.0.5.3", {"start": v(10, 9.4) * mm, "end": v(10, 8.6) * mm});
            skLineSegment(sketch, "E84.0.6.0", {"start": v(11, 7.5) * mm, "end": v(10, 7.4) * mm});
            skLineSegment(sketch, "E84.0.6.1", {"start": v(11, 6.5) * mm, "end": v(11, 7.5) * mm});
            skLineSegment(sketch, "E84.0.6.2", {"start": v(10, 6.6) * mm, "end": v(11, 6.5) * mm});
            skLineSegment(sketch, "E84.0.6.3", {"start": v(10, 7.4) * mm, "end": v(10, 6.6) * mm});
            skLineSegment(sketch, "E84.0.7.0", {"start": v(11, 5.5) * mm, "end": v(10, 5.4) * mm});
            skLineSegment(sketch, "E84.0.7.1", {"start": v(11, 4.5) * mm, "end": v(11, 5.5) * mm});
            skLineSegment(sketch, "E84.0.7.2", {"start": v(10, 4.6) * mm, "end": v(11, 4.5) * mm});
            skLineSegment(sketch, "E84.0.7.3", {"start": v(10, 5.4) * mm, "end": v(10, 4.6) * mm});
            skLineSegment(sketch, "E84.0.8.0", {"start": v(11, 3.5) * mm, "end": v(10, 3.4) * mm});
            skLineSegment(sketch, "E84.0.8.1", {"start": v(11, 2.5) * mm, "end": v(11, 3.5) * mm});
            skLineSegment(sketch, "E84.0.8.2", {"start": v(10, 2.6) * mm, "end": v(11, 2.5) * mm});
            skLineSegment(sketch, "E84.0.8.3", {"start": v(10, 3.4) * mm, "end": v(10, 2.6) * mm});
            skLineSegment(sketch, "E84.0.9.0", {"start": v(11, 1.5) * mm, "end": v(10, 1.4) * mm});
            skLineSegment(sketch, "E84.0.9.1", {"start": v(11, 0.5) * mm, "end": v(11, 1.5) * mm});
            skLineSegment(sketch, "E84.0.9.2", {"start": v(10, 0.6) * mm, "end": v(11, 0.5) * mm});
            skLineSegment(sketch, "E84.0.9.3", {"start": v(10, 1.4) * mm, "end": v(10, 0.6) * mm});
            skLineSegment(sketch, "E84.direction1", {"start": v(11, 19.5) * mm, "end": v(36, 19.5) * mm, "construction": true});
            skLineSegment(sketch, "E84.direction2", {"start": v(11, 19.5) * mm, "end": v(11, 17.5) * mm, "construction": true});
            skSolve(sketch);
        }
        {
            var Q0;
            Q0=qSketchRegion(id+"F31",true);
            extrude(context, id + "F32", {"entities" : qUnion([Q0]), "operationType" : NewBodyOperationType.ADD, "depth" : 8 * mm});
        }
        {
            var Q0;
            Q0=makeQuery(id+"F4.opExtrude","SWEPT_FACE",FACE,{"disambiguationData":[OSD([sQuery(id+"F3.wireOp",EDGE,"E14")])]});
            var sketch = newSketch(context, id + "F33", { "sketchPlane" : qUnion([Q0])});
            skLineSegment(sketch, "E85", {"start": v(35, 10) * mm, "end": v(31, 10) * mm, "construction": true});
            skCircle(sketch, "E86", {"center": v(31, 10) * mm, "radius": 1.7 * mm});
            skSolve(sketch);
        }
        {
            var Q0;
            Q0=qSketchRegion(id+"F33",true);
            var Q1;
            Q1=makeQuery(id+"F4.opExtrude","SWEPT_FACE",FACE,{"disambiguationData":[OSD([sQuery(id+"F3.wireOp",EDGE,"E10")])]});
            extrude(context, id + "F34", {"entities" : qUnion([Q0]), "operationType" : NewBodyOperationType.REMOVE, "endBound" : BoundingType.UP_TO_SURFACE, "oppositeDirection" : true, "endBoundEntityFace" : qUnion([Q1]), "depth" : 25 * mm});
        }
        {
            var Q0;
            {var subQ0=sQuery(id+"F0.wireOp",EDGE,"E0");var subQ1=sQuery(id+"F0.wireOp",EDGE,"E1");var subQ2=sQuery(id+"F0.wireOp",EDGE,"E2");Q0=makeQuery(id+"F19.boolean.opBoolean","MERGE",FACE,{"derivedFrom":[makeQuery(id+"F8.boolean.opBoolean","SPLIT",FACE,{"disambiguationData":[TD([makeQuery(id+"F1.opExtrude","SWEPT_FACE",FACE,{"disambiguationData":[OSD([subQ0])]})])],"derivedFrom":makeQuery(id+"F1.opExtrude","CAP_FACE",FACE,{"disambiguationData":[OSD([subQ0,subQ1,subQ2,sQuery(id+"F0.wireOp",EDGE,"E3")])],"isStart":false})}),makeQuery(id+"F19.opExtrude","CAP_FACE",FACE,{"disambiguationData":[OSD([sQuery(id+"F18.wireOp",EDGE,"E59.0"),sQuery(id+"F18.wireOp",EDGE,"E60.0"),sQuery(id+"F18.wireOp",EDGE,"E61.0"),sQuery(id+"F18.wireOp",EDGE,"E62.0")])],"isStart":true})]});}
            var sketch = newSketch(context, id + "F35", { "sketchPlane" : qUnion([Q0])});
            skLineSegment(sketch, "E87.0", {"start": v(-35, -9) * mm, "end": v(-35, 2) * mm});
            skLineSegment(sketch, "E88.0", {"start": v(-19.3, -9) * mm, "end": v(-35, -9) * mm});
            skLineSegment(sketch, "E89.0", {"start": v(-19.3, -11) * mm, "end": v(-19.3, -9) * mm});
            skLineSegment(sketch, "E90.0", {"start": v(-35, -11) * mm, "end": v(-19.3, -11) * mm});
            skLineSegment(sketch, "E91.0", {"start": v(-35, -22) * mm, "end": v(-35, -11) * mm});
            skLineSegment(sketch, "E92.0", {"start": v(-12, -22) * mm, "end": v(-35, -22) * mm});
            skLineSegment(sketch, "E93", {"start": v(-12, -22) * mm, "end": v(-12, 2) * mm});
            skLineSegment(sketch, "E94", {"start": v(-12, 2) * mm, "end": v(-35, 2) * mm});
            skSolve(sketch);
        }
        {
            var Q0;
            Q0=qSketchRegion(id+"F35",true);
            extrude(context, id + "F36", {"entities" : qUnion([Q0]), "oppositeDirection" : true, "depth" : 15 * mm});
        }
        {
            var Q0;
            Q0=makeQuery(id+"F36.opExtrude","CAP_FACE",FACE,{"disambiguationData":[OSD([sQuery(id+"F35.wireOp",EDGE,"E87.0"),sQuery(id+"F35.wireOp",EDGE,"E88.0"),sQuery(id+"F35.wireOp",EDGE,"E89.0"),sQuery(id+"F35.wireOp",EDGE,"E90.0"),sQuery(id+"F35.wireOp",EDGE,"E91.0"),sQuery(id+"F35.wireOp",EDGE,"E92.0"),sQuery(id+"F35.wireOp",EDGE,"E93"),sQuery(id+"F35.wireOp",EDGE,"E94")])],"isStart":true});
            var sketch = newSketch(context, id + "F37", { "sketchPlane" : qUnion([Q0])});
            skCircle(sketch, "E95.0", {"center": v(-23.1, -16) * mm, "radius": 1.6 * mm});
            skCircle(sketch, "E96.0", {"center": v(-23.1, -4) * mm, "radius": 1.6 * mm});
            skSolve(sketch);
        }
        {
            var Q0;
            Q0=qSketchRegion(id+"F37",true);
            extrude(context, id + "F38", {"entities" : qUnion([Q0]), "operationType" : NewBodyOperationType.REMOVE, "endBound" : BoundingType.THROUGH_ALL, "oppositeDirection" : true, "depth" : 25 * mm});
        }
        {
            var Q0;
            Q0=makeQuery(id+"F36.opExtrude","SWEPT_FACE",FACE,{"disambiguationData":[OSD([sQuery(id+"F35.wireOp",EDGE,"E89.0")])]});
            var sketch = newSketch(context, id + "F39", { "sketchPlane" : qUnion([Q0])});
            skLineSegment(sketch, "E97", {"start": v(11, 27) * mm, "end": v(10, 26.9) * mm});
            skLineSegment(sketch, "E98", {"start": v(10, 26.9) * mm, "end": v(10, 26.1) * mm});
            skLineSegment(sketch, "E99", {"start": v(10, 26.1) * mm, "end": v(11, 26) * mm});
            skLineSegment(sketch, "E100", {"start": v(11, 26) * mm, "end": v(11, 27) * mm});
            skLineSegment(sketch, "E101", {"start": v(10, 26.5) * mm, "end": v(11, 26.5) * mm, "construction": true});
            skLineSegment(sketch, "E102.0.1.0", {"start": v(10, 28.1) * mm, "end": v(11, 28) * mm});
            skLineSegment(sketch, "E102.0.1.1", {"start": v(11, 28) * mm, "end": v(11, 29) * mm});
            skLineSegment(sketch, "E102.0.1.2", {"start": v(11, 29) * mm, "end": v(10, 28.9) * mm});
            skLineSegment(sketch, "E102.0.1.3", {"start": v(10, 28.9) * mm, "end": v(10, 28.1) * mm});
            skLineSegment(sketch, "E102.0.2.0", {"start": v(10, 30.1) * mm, "end": v(11, 30) * mm});
            skLineSegment(sketch, "E102.0.2.1", {"start": v(11, 30) * mm, "end": v(11, 31) * mm});
            skLineSegment(sketch, "E102.0.2.2", {"start": v(11, 31) * mm, "end": v(10, 30.9) * mm});
            skLineSegment(sketch, "E102.0.2.3", {"start": v(10, 30.9) * mm, "end": v(10, 30.1) * mm});
            skLineSegment(sketch, "E102.0.3.0", {"start": v(10, 32.1) * mm, "end": v(11, 32) * mm});
            skLineSegment(sketch, "E102.0.3.1", {"start": v(11, 32) * mm, "end": v(11, 33) * mm});
            skLineSegment(sketch, "E102.0.3.2", {"start": v(11, 33) * mm, "end": v(10, 32.9) * mm});
            skLineSegment(sketch, "E102.0.3.3", {"start": v(10, 32.9) * mm, "end": v(10, 32.1) * mm});
            skLineSegment(sketch, "E102.0.4.0", {"start": v(10, 34.1) * mm, "end": v(11, 34) * mm});
            skLineSegment(sketch, "E102.0.4.1", {"start": v(11, 34) * mm, "end": v(11, 35) * mm});
            skLineSegment(sketch, "E102.0.4.2", {"start": v(11, 35) * mm, "end": v(10, 34.9) * mm});
            skLineSegment(sketch, "E102.0.4.3", {"start": v(10, 34.9) * mm, "end": v(10, 34.1) * mm});
            skLineSegment(sketch, "E102.0.5.0", {"start": v(10, 36.1) * mm, "end": v(11, 36) * mm});
            skLineSegment(sketch, "E102.0.5.1", {"start": v(11, 36) * mm, "end": v(11, 37) * mm});
            skLineSegment(sketch, "E102.0.5.2", {"start": v(11, 37) * mm, "end": v(10, 36.9) * mm});
            skLineSegment(sketch, "E102.0.5.3", {"start": v(10, 36.9) * mm, "end": v(10, 36.1) * mm});
            skLineSegment(sketch, "E102.0.6.0", {"start": v(10, 38.1) * mm, "end": v(11, 38) * mm});
            skLineSegment(sketch, "E102.0.6.1", {"start": v(11, 38) * mm, "end": v(11, 39) * mm});
            skLineSegment(sketch, "E102.0.6.2", {"start": v(11, 39) * mm, "end": v(10, 38.9) * mm});
            skLineSegment(sketch, "E102.0.6.3", {"start": v(10, 38.9) * mm, "end": v(10, 38.1) * mm});
            skLineSegment(sketch, "E102.direction1", {"start": v(10, 26.1) * mm, "end": v(35, 26.1) * mm, "construction": true});
            skLineSegment(sketch, "E102.direction2", {"start": v(10, 26.1) * mm, "end": v(10, 28.1) * mm, "construction": true});
            skSolve(sketch);
        }
        {
            var Q0;
            Q0=qSketchRegion(id+"F39",true);
            var Q1;
            Q1=makeQuery(id+"F32.opExtrude","CAP_FACE",FACE,{"disambiguationData":[OSD([sQuery(id+"F31.wireOp",EDGE,"E80"),sQuery(id+"F31.wireOp",EDGE,"E81"),sQuery(id+"F31.wireOp",EDGE,"E82"),sQuery(id+"F31.wireOp",EDGE,"E83")])],"isStart":false});
            extrude(context, id + "F40", {"entities" : qUnion([Q0]), "operationType" : NewBodyOperationType.ADD, "endBound" : BoundingType.UP_TO_SURFACE, "endBoundEntityFace" : qUnion([Q1]), "depth" : 25 * mm});
        }
        {
            var Q0;
            Q0=makeQuery(id+"F36.opExtrude","SWEPT_FACE",FACE,{"disambiguationData":[OSD([sQuery(id+"F35.wireOp",EDGE,"E92.0")])]});
            var sketch = newSketch(context, id + "F41", { "sketchPlane" : qUnion([Q0])});
            skCircle(sketch, "E103.0", {"center": v(-31, 10) * mm, "radius": 1.7 * mm, "construction": true});
            skLineSegment(sketch, "E104", {"start": v(-31, 10) * mm, "end": v(-31, 32.5) * mm, "construction": true});
            skPoint(sketch, "E104.endSnap0", {"position": v(-35, 32.5) * mm});
            skLineSegment(sketch, "E105", {"start": v(-31, 32.5) * mm, "end": v(-35, 32.5) * mm, "construction": true});
            skCircle(sketch, "E106", {"center": v(-31, 32.5) * mm, "radius": 1.7 * mm});
            skSolve(sketch);
        }
        {
            var Q0;
            Q0=qSketchRegion(id+"F41",true);
            extrude(context, id + "F42", {"entities" : qUnion([Q0]), "operationType" : NewBodyOperationType.REMOVE, "endBound" : BoundingType.THROUGH_ALL, "oppositeDirection" : true, "depth" : 25 * mm});
        }
        {
            var Q0;
            Q0=makeQuery(id+"F23.boolean.opBoolean","COPY",EDGE,{"derivedFrom":makeQuery(id+"F23.opExtrude","CAP_EDGE",EDGE,{"disambiguationData":[OSD([sQuery(id+"F22.wireOp",EDGE,"E65.0.1")])],"isStart":true})});
            var Q1;
            Q1=makeQuery(id+"F23.boolean.opBoolean","COPY",EDGE,{"derivedFrom":makeQuery(id+"F23.opExtrude","CAP_EDGE",EDGE,{"disambiguationData":[OSD([sQuery(id+"F22.wireOp",EDGE,"E65.0.0")])],"isStart":true})});
            var Q2;
            Q2=makeQuery(id+"F23.boolean.opBoolean","COPY",EDGE,{"derivedFrom":makeQuery(id+"F23.opExtrude","CAP_EDGE",EDGE,{"disambiguationData":[OSD([sQuery(id+"F22.wireOp",EDGE,"E65.0.3")])],"isStart":true})});
            var Q3;
            Q3=makeQuery(id+"F23.boolean.opBoolean","COPY",EDGE,{"derivedFrom":makeQuery(id+"F23.opExtrude","CAP_EDGE",EDGE,{"disambiguationData":[OSD([sQuery(id+"F22.wireOp",EDGE,"E65.0.2")])],"isStart":true})});
            var Q4;
            Q4=makeQuery(id+"F8.boolean.opBoolean","COPY",EDGE,{"derivedFrom":makeQuery(id+"F8.opExtrude","CAP_EDGE",EDGE,{"disambiguationData":[OSD([sQuery(id+"F7.wireOp",EDGE,"E28")])],"isStart":true})});
            var Q5;
            Q5=makeQuery(id+"F8.boolean.opBoolean","COPY",EDGE,{"disambiguationData":[OD(0.0)],"derivedFrom":makeQuery(id+"F8.opExtrude","SWEPT_EDGE",EDGE,{"disambiguationData":[OSD([sQuery(id+"F0.wireOp",EDGE,"E1"),sQuery(id+"F7.wireOp",EDGE,"E26"),sQuery(id+"F7.wireOp",EDGE,"E28")])]})});
            var Q6;
            {var subQ0=sQuery(id+"F5.wireOp",EDGE,"E22");Q6=makeQuery(id+"F8.boolean.opBoolean","SPLIT",EDGE,{"disambiguationData":[TD([makeQuery(id+"F8.opExtrude","SWEPT_FACE",FACE,{"disambiguationData":[OSD([sQuery(id+"F7.wireOp",EDGE,"E28")])]})])],"derivedFrom":makeQuery(id+"F6.boolean.opBoolean","COPY",EDGE,{"derivedFrom":makeQuery(id+"F6.opExtrude","CAP_EDGE",EDGE,{"disambiguationData":[OSD([subQ0])],"isStart":true})})});}
            var Q7;
            Q7=makeQuery(id+"F8.boolean.opBoolean","INTERSECT",EDGE,{"disambiguationData":[OD(1.0)],"derivedFrom":[makeQuery(id+"F6.boolean.opBoolean","COPY",FACE,{"derivedFrom":makeQuery(id+"F6.opExtrude","SWEPT_FACE",FACE,{"disambiguationData":[OSD([sQuery(id+"F5.wireOp",EDGE,"E22")])]})}),makeQuery(id+"F8.opExtrude","SWEPT_FACE",FACE,{"disambiguationData":[OSD([sQuery(id+"F7.wireOp",EDGE,"E28")])]})]});
            var Q8;
            Q8=makeQuery(id+"F8.boolean.opBoolean","INTERSECT",EDGE,{"disambiguationData":[OD(0.0)],"derivedFrom":[makeQuery(id+"F6.boolean.opBoolean","COPY",FACE,{"derivedFrom":makeQuery(id+"F6.opExtrude","SWEPT_FACE",FACE,{"disambiguationData":[OSD([sQuery(id+"F5.wireOp",EDGE,"E22")])]})}),makeQuery(id+"F8.opExtrude","SWEPT_FACE",FACE,{"disambiguationData":[OSD([sQuery(id+"F7.wireOp",EDGE,"E28")])]})]});
            var Q9;
            Q9=makeQuery(id+"F4.opExtrude","CAP_EDGE",EDGE,{"disambiguationData":[OSD([sQuery(id+"F3.wireOp",EDGE,"E10")])],"isStart":true});
            var Q10;
            Q10=makeQuery(id+"F8.boolean.opBoolean","COPY",EDGE,{"derivedFrom":makeQuery(id+"F8.opExtrude","SWEPT_EDGE",EDGE,{"disambiguationData":[OSD([sQuery(id+"F3.wireOp",EDGE,"E10"),sQuery(id+"F7.wireOp",EDGE,"E31"),sQuery(id+"F7.wireOp",EDGE,"E32")])]})});
            var Q11;
            Q11=makeQuery(id+"F4.opExtrude","TWEAK_EDGE",EDGE,{"derivedFrom":[dummyQuery(id+"F2.planeOp",FACE),makeQuery(id+"F3.imprint","IMPRINT",EDGE,{"derivedFrom":sQuery(id+"F3.wireOp",EDGE,"E10")})]});
            var Q12;
            Q12=makeQuery(id+"F4.opExtrude","SWEPT_EDGE",EDGE,{"disambiguationData":[OSD([sQuery(id+"F3.wireOp",EDGE,"E9"),sQuery(id+"F3.wireOp",EDGE,"E10")])]});
            var Q13;
            Q13=makeQuery(id+"F4.opExtrude","CAP_EDGE",EDGE,{"disambiguationData":[OSD([sQuery(id+"F3.wireOp",EDGE,"E9")])],"isStart":true});
            var Q14;
            Q14=makeQuery(id+"F4.opExtrude","TWEAK_EDGE",EDGE,{"derivedFrom":[dummyQuery(id+"F2.planeOp",FACE),makeQuery(id+"F3.imprint","IMPRINT",EDGE,{"derivedFrom":sQuery(id+"F3.wireOp",EDGE,"E9")})]});
            var Q15;
            Q15=makeQuery(id+"F4.opExtrude","SWEPT_EDGE",EDGE,{"disambiguationData":[OSD([sQuery(id+"F3.wireOp",EDGE,"E8"),sQuery(id+"F3.wireOp",EDGE,"E9")])]});
            var Q16;
            Q16=makeQuery(id+"F4.opExtrude","SWEPT_EDGE",EDGE,{"disambiguationData":[OSD([sQuery(id+"F3.wireOp",EDGE,"E5"),sQuery(id+"F3.wireOp",EDGE,"E6")])]});
            var Q17;
            Q17=makeQuery(id+"F4.opExtrude","TWEAK_EDGE",EDGE,{"derivedFrom":[dummyQuery(id+"F2.planeOp",FACE),makeQuery(id+"F3.imprint","IMPRINT",EDGE,{"derivedFrom":sQuery(id+"F3.wireOp",EDGE,"E5")})]});
            var Q18;
            Q18=makeQuery(id+"F4.opExtrude","CAP_EDGE",EDGE,{"disambiguationData":[OSD([sQuery(id+"F3.wireOp",EDGE,"E5")])],"isStart":true});
            var Q19;
            Q19=makeQuery(id+"F4.opExtrude","SWEPT_EDGE",EDGE,{"disambiguationData":[OSD([sQuery(id+"F3.wireOp",EDGE,"E5"),sQuery(id+"F3.wireOp",EDGE,"E14")])]});
            var Q20;
            Q20=makeQuery(id+"F4.opExtrude","CAP_EDGE",EDGE,{"disambiguationData":[OSD([sQuery(id+"F3.wireOp",EDGE,"E6")])],"isStart":true});
            var Q21;
            Q21=makeQuery(id+"F4.opExtrude","CAP_EDGE",EDGE,{"disambiguationData":[OSD([sQuery(id+"F3.wireOp",EDGE,"E14")])],"isStart":true});
            var Q22;
            Q22=makeQuery(id+"F17.opExtrude","CAP_EDGE",EDGE,{"disambiguationData":[OSD([sQuery(id+"F16.wireOp",EDGE,"E49")])],"isStart":true});
            var Q23;
            {var subQ0=sQuery(id+"F3.wireOp",EDGE,"E10");var subQ1=sQuery(id+"F3.wireOp",EDGE,"E9");var subQ2=sQuery(id+"F3.wireOp",EDGE,"E8");var subQ3=sQuery(id+"F3.wireOp",EDGE,"E7");var subQ4=sQuery(id+"F0.wireOp",EDGE,"E1");var subQ5=sQuery(id+"F0.wireOp",EDGE,"E0");var subQ6=sQuery(id+"F3.wireOp",EDGE,"5d72e0aa-44b3-420c-8565-5770b2da08a5");var subQ7=sQuery(id+"F3.wireOp",EDGE,"E14");var subQ8=sQuery(id+"F3.wireOp",EDGE,"E5");var subQ9=sQuery(id+"F3.wireOp",EDGE,"E6");Q23=makeQuery(id+"F13.opFillet","BLEND_EDGE",EDGE,{"blendedFrom":[makeQuery(id+"F1.opExtrude","SWEPT_EDGE",EDGE,{"disambiguationData":[OSD([subQ5,subQ4])]}),makeQuery(id+"F8.boolean.opBoolean","SPLIT",FACE,{"disambiguationData":[TD([makeQuery(id+"F1.opExtrude","SWEPT_FACE",FACE,{"disambiguationData":[OSD([subQ5])]})])],"derivedFrom":makeQuery(id+"F4.boolean.opBoolean","MERGE",FACE,{"derivedFrom":[makeQuery(id+"F1.opExtrude","CAP_FACE",FACE,{"disambiguationData":[OSD([subQ5,subQ4,sQuery(id+"F0.wireOp",EDGE,"E2"),sQuery(id+"F0.wireOp",EDGE,"E3")])],"isStart":true}),makeQuery(id+"F4.opExtrude","CAP_FACE",FACE,{"disambiguationData":[OSD([subQ8,subQ9,subQ3,subQ2,subQ1,subQ0,sQuery(id+"F3.wireOp",EDGE,"E11"),sQuery(id+"F3.wireOp",EDGE,"bca63a35-03c2-4865-813d-011e51dad5aa"),subQ7,subQ6])],"isStart":true})]})})],"blendedInto":[makeQuery(id+"F8.boolean.opBoolean","SPLIT",FACE,{"disambiguationData":[TD([makeQuery(id+"F1.opExtrude","SWEPT_FACE",FACE,{"disambiguationData":[OSD([subQ5])]})])],"derivedFrom":makeQuery(id+"F4.boolean.opBoolean","MERGE",FACE,{"derivedFrom":[makeQuery(id+"F1.opExtrude","CAP_FACE",FACE,{"disambiguationData":[OSD([subQ5,subQ4,sQuery(id+"F0.wireOp",EDGE,"E2"),sQuery(id+"F0.wireOp",EDGE,"E3")])],"isStart":true}),makeQuery(id+"F4.opExtrude","CAP_FACE",FACE,{"disambiguationData":[OSD([subQ8,subQ9,subQ3,subQ2,subQ1,subQ0,sQuery(id+"F3.wireOp",EDGE,"E11"),sQuery(id+"F3.wireOp",EDGE,"bca63a35-03c2-4865-813d-011e51dad5aa"),subQ7,subQ6])],"isStart":true})]})})]});}
            var Q24;
            {var subQ0=sQuery(id+"F0.wireOp",EDGE,"E0");var subQ1=sQuery(id+"F0.wireOp",EDGE,"E1");var subQ2=sQuery(id+"F0.wireOp",EDGE,"E2");Q24=makeQuery(id+"F13.opFillet","BLEND_EDGE",EDGE,{"blendedFrom":[makeQuery(id+"F1.opExtrude","SWEPT_EDGE",EDGE,{"disambiguationData":[OSD([subQ0,subQ1])]}),makeQuery(id+"F8.boolean.opBoolean","SPLIT",FACE,{"disambiguationData":[TD([makeQuery(id+"F1.opExtrude","SWEPT_FACE",FACE,{"disambiguationData":[OSD([subQ0])]})])],"derivedFrom":makeQuery(id+"F1.opExtrude","CAP_FACE",FACE,{"disambiguationData":[OSD([subQ0,subQ1,subQ2,sQuery(id+"F0.wireOp",EDGE,"E3")])],"isStart":false})})],"blendedInto":[makeQuery(id+"F8.boolean.opBoolean","SPLIT",FACE,{"disambiguationData":[TD([makeQuery(id+"F1.opExtrude","SWEPT_FACE",FACE,{"disambiguationData":[OSD([subQ0])]})])],"derivedFrom":makeQuery(id+"F1.opExtrude","CAP_FACE",FACE,{"disambiguationData":[OSD([subQ0,subQ1,subQ2,sQuery(id+"F0.wireOp",EDGE,"E3")])],"isStart":false})})]});}
            var Q25;
            Q25=makeQuery(id+"F8.boolean.opBoolean","COPY",EDGE,{"disambiguationData":[OD(1.0)],"derivedFrom":makeQuery(id+"F8.opExtrude","SWEPT_EDGE",EDGE,{"disambiguationData":[OSD([sQuery(id+"F0.wireOp",EDGE,"E1"),sQuery(id+"F7.wireOp",EDGE,"E26"),sQuery(id+"F7.wireOp",EDGE,"E28")])]})});
            var Q26;
            Q26=makeQuery(id+"F8.boolean.opBoolean","COPY",EDGE,{"disambiguationData":[OD(1.0)],"derivedFrom":makeQuery(id+"F8.opExtrude","SWEPT_EDGE",EDGE,{"disambiguationData":[OSD([sQuery(id+"F7.wireOp",EDGE,"E28"),sQuery(id+"F7.wireOp",EDGE,"E33.filletArc")])]})});
            var Q27;
            Q27=makeQuery(id+"F8.boolean.opBoolean","INTERSECT",EDGE,{"derivedFrom":[makeQuery(id+"F1.opExtrude","CAP_FACE",FACE,{"disambiguationData":[OSD([sQuery(id+"F0.wireOp",EDGE,"E0"),sQuery(id+"F0.wireOp",EDGE,"E1"),sQuery(id+"F0.wireOp",EDGE,"E2"),sQuery(id+"F0.wireOp",EDGE,"E3")])],"isStart":false}),makeQuery(id+"F8.opExtrude","SWEPT_FACE",FACE,{"disambiguationData":[OSD([sQuery(id+"F7.wireOp",EDGE,"E28")])]})]});
            var Q28;
            Q28=makeQuery(id+"F8.boolean.opBoolean","INTERSECT",EDGE,{"derivedFrom":[makeQuery(id+"F4.opExtrude","CAP_FACE",FACE,{"disambiguationData":[OSD([dummyQuery(id+"F2.planeOp",FACE)])],"isStart":false}),makeQuery(id+"F8.opExtrude","SWEPT_FACE",FACE,{"disambiguationData":[OSD([sQuery(id+"F7.wireOp",EDGE,"E32")])]})]});
            var Q29;
            Q29=makeQuery(id+"F6.boolean.opBoolean","INTERSECT",EDGE,{"disambiguationData":[OD(0.0)],"derivedFrom":[makeQuery(id+"F4.opExtrude","CAP_FACE",FACE,{"disambiguationData":[OSD([dummyQuery(id+"F2.planeOp",FACE)])],"isStart":false}),makeQuery(id+"F6.opExtrude","SWEPT_FACE",FACE,{"disambiguationData":[OSD([sQuery(id+"F5.wireOp",EDGE,"E22")])]})]});
            var Q30;
            Q30=makeQuery(id+"F8.boolean.opBoolean","SPLIT",EDGE,{"derivedFrom":makeQuery(id+"F6.boolean.opBoolean","INTERSECT",EDGE,{"derivedFrom":[makeQuery(id+"F1.opExtrude","SWEPT_FACE",FACE,{"disambiguationData":[OSD([sQuery(id+"F0.wireOp",EDGE,"E2")])]}),makeQuery(id+"F6.opExtrude","SWEPT_FACE",FACE,{"disambiguationData":[OSD([sQuery(id+"F5.wireOp",EDGE,"E22")])]})]})});
            var Q31;
            {var subQ0=dummyQuery(id+"F2.planeOp",FACE);Q31=makeQuery(id+"F6.boolean.opBoolean","SPLIT",EDGE,{"disambiguationData":[TD([makeQuery(id+"F1.opExtrude","SWEPT_FACE",FACE,{"disambiguationData":[OSD([sQuery(id+"F0.wireOp",EDGE,"E0")])]})])],"derivedFrom":makeQuery(id+"F4.opExtrude","TWEAK_EDGE",EDGE,{"derivedFrom":[subQ0,makeQuery(id+"F3.imprint","IMPRINT",EDGE,{"derivedFrom":sQuery(id+"F3.wireOp",EDGE,"E11")})]})});}
            var Q32;
            Q32=makeQuery(id+"F4.opExtrude","TWEAK_EDGE",EDGE,{"derivedFrom":[dummyQuery(id+"F2.planeOp",FACE),makeQuery(id+"F3.imprint","IMPRINT",EDGE,{"derivedFrom":sQuery(id+"F3.wireOp",EDGE,"bca63a35-03c2-4865-813d-011e51dad5aa")})]});
            var Q33;
            Q33=makeQuery(id+"F1.opExtrude","SWEPT_EDGE",EDGE,{"disambiguationData":[OSD([sQuery(id+"F0.wireOp",EDGE,"E0"),sQuery(id+"F0.wireOp",EDGE,"E2")])]});
            var Q34;
            {var subQ0=sQuery(id+"F0.wireOp",EDGE,"E2");var subQ1=sQuery(id+"F0.wireOp",EDGE,"E0");Q34=makeQuery(id+"F8.boolean.opBoolean","SPLIT",EDGE,{"disambiguationData":[TD([makeQuery(id+"F1.opExtrude","SWEPT_FACE",FACE,{"disambiguationData":[OSD([subQ1])]})])],"derivedFrom":makeQuery(id+"F1.opExtrude","CAP_EDGE",EDGE,{"disambiguationData":[OSD([subQ0])],"isStart":false})});}
            var Q35;
            {var subQ0=sQuery(id+"F0.wireOp",EDGE,"E0");var subQ1=sQuery(id+"F0.wireOp",EDGE,"E2");Q35=makeQuery(id+"F12.boolean.opBoolean","SPLIT",EDGE,{"disambiguationData":[TD([makeQuery(id+"F8.boolean.opBoolean","COPY",FACE,{"derivedFrom":makeQuery(id+"F1.opExtrude","SWEPT_FACE",FACE,{"disambiguationData":[OSD([subQ1])]})})])],"derivedFrom":makeQuery(id+"F1.opExtrude","CAP_EDGE",EDGE,{"disambiguationData":[OSD([subQ0])],"isStart":false})});}
            var Q36;
            Q36=makeQuery(id+"F4.opExtrude","TWEAK_EDGE",EDGE,{"derivedFrom":[dummyQuery(id+"F2.planeOp",FACE),makeQuery(id+"F3.imprint","IMPRINT",EDGE,{"derivedFrom":sQuery(id+"F3.wireOp",EDGE,"E14")})]});
            var Q37;
            Q37=makeQuery(id+"F4.opExtrude","TWEAK_EDGE",EDGE,{"derivedFrom":[dummyQuery(id+"F2.planeOp",FACE),makeQuery(id+"F3.imprint","IMPRINT",EDGE,{"derivedFrom":sQuery(id+"F3.wireOp",EDGE,"E8")})]});
            var Q38;
            Q38=makeQuery(id+"F4.opExtrude","TWEAK_EDGE",EDGE,{"derivedFrom":[dummyQuery(id+"F2.planeOp",FACE),makeQuery(id+"F3.imprint","IMPRINT",EDGE,{"derivedFrom":sQuery(id+"F3.wireOp",EDGE,"E6")})]});
            var Q39;
            Q39=makeQuery(id+"F4.opExtrude","CAP_EDGE",EDGE,{"disambiguationData":[OSD([sQuery(id+"F3.wireOp",EDGE,"E8")])],"isStart":true});
            var Q40;
            Q40=makeQuery(id+"F4.opExtrude","CAP_EDGE",EDGE,{"disambiguationData":[OSD([sQuery(id+"F3.wireOp",EDGE,"E7")])],"isStart":true});
            var Q41;
            Q41=makeQuery(id+"F4.opExtrude","TWEAK_EDGE",EDGE,{"derivedFrom":[dummyQuery(id+"F2.planeOp",FACE),makeQuery(id+"F3.imprint","IMPRINT",EDGE,{"derivedFrom":sQuery(id+"F3.wireOp",EDGE,"E7")})]});
            var Q42;
            Q42=makeQuery(id+"F19.opExtrude","CAP_EDGE",EDGE,{"disambiguationData":[OSD([sQuery(id+"F18.wireOp",EDGE,"E59.0")])],"isStart":true});
            var Q43;
            Q43=makeQuery(id+"F19.opExtrude","SWEPT_EDGE",EDGE,{"disambiguationData":[OSD([sQuery(id+"F18.wireOp",EDGE,"E59.0"),sQuery(id+"F18.wireOp",EDGE,"E61.0")])]});
            var Q44;
            Q44=makeQuery(id+"F19.opExtrude","CAP_EDGE",EDGE,{"disambiguationData":[OSD([sQuery(id+"F18.wireOp",EDGE,"E61.0")])],"isStart":true});
            var Q45;
            Q45=makeQuery(id+"F19.opExtrude","CAP_EDGE",EDGE,{"disambiguationData":[OSD([sQuery(id+"F18.wireOp",EDGE,"E60.0")])],"isStart":true});
            var Q46;
            Q46=makeQuery(id+"F19.opExtrude","SWEPT_EDGE",EDGE,{"disambiguationData":[OSD([sQuery(id+"F18.wireOp",EDGE,"E59.0"),sQuery(id+"F18.wireOp",EDGE,"E60.0")])]});
            var Q47;
            Q47=makeQuery(id+"F17.opExtrude","SWEPT_EDGE",EDGE,{"disambiguationData":[OSD([sQuery(id+"F16.wireOp",EDGE,"E49"),sQuery(id+"F16.wireOp",EDGE,"E55")])]});
            var Q48;
            Q48=makeQuery(id+"F17.opExtrude","CAP_EDGE",EDGE,{"disambiguationData":[OSD([sQuery(id+"F16.wireOp",EDGE,"E55")])],"isStart":true});
            var Q49;
            Q49=makeQuery(id+"F17.opExtrude","CAP_EDGE",EDGE,{"disambiguationData":[OSD([sQuery(id+"F16.wireOp",EDGE,"E56")])],"isStart":true});
            var Q50;
            Q50=makeQuery(id+"F17.opExtrude","SWEPT_EDGE",EDGE,{"disambiguationData":[OSD([sQuery(id+"F16.wireOp",EDGE,"E49"),sQuery(id+"F16.wireOp",EDGE,"E56")])]});
            var Q51;
            {var subQ0=sQuery(id+"F9.wireOp",EDGE,"E34");var subQ1=sQuery(id+"F11.wireOp",EDGE,"E37");Q51=makeQuery(id+"F17.boolean.opBoolean","MERGE",EDGE,{"derivedFrom":[makeQuery(id+"F15.boolean.opBoolean","SPLIT",EDGE,{"disambiguationData":[TD([makeQuery(id+"F15.opExtrude","SWEPT_FACE",FACE,{"disambiguationData":[OSD([sQuery(id+"F14.wireOp",EDGE,"E43.rect.top")])]})])],"derivedFrom":makeQuery(id+"F12.boolean.opBoolean","COPY",EDGE,{"derivedFrom":makeQuery(id+"F12.opExtrude","SWEPT_EDGE",EDGE,{"disambiguationData":[OSD([subQ0,subQ1,sQuery(id+"F11.wireOp",EDGE,"E42")])]})})}),makeQuery(id+"F17.opExtrude","SWEPT_EDGE",EDGE,{"disambiguationData":[OSD([sQuery(id+"F16.wireOp",EDGE,"E50.0"),sQuery(id+"F16.wireOp",EDGE,"E54"),sQuery(id+"F16.wireOp",EDGE,"E56")])]})]});}
            var Q52;
            {var subQ0=sQuery(id+"F9.wireOp",EDGE,"E34");var subQ1=sQuery(id+"F11.wireOp",EDGE,"E39");Q52=makeQuery(id+"F17.boolean.opBoolean","MERGE",EDGE,{"derivedFrom":[makeQuery(id+"F15.boolean.opBoolean","SPLIT",EDGE,{"disambiguationData":[TD([makeQuery(id+"F15.opExtrude","SWEPT_FACE",FACE,{"disambiguationData":[OSD([sQuery(id+"F14.wireOp",EDGE,"E43.rect.top")])]})])],"derivedFrom":makeQuery(id+"F12.boolean.opBoolean","COPY",EDGE,{"derivedFrom":makeQuery(id+"F12.opExtrude","SWEPT_EDGE",EDGE,{"disambiguationData":[OSD([subQ0,subQ1,sQuery(id+"F11.wireOp",EDGE,"E42")])]})})}),makeQuery(id+"F17.opExtrude","SWEPT_EDGE",EDGE,{"disambiguationData":[OSD([sQuery(id+"F16.wireOp",EDGE,"E50.0"),sQuery(id+"F16.wireOp",EDGE,"E53"),sQuery(id+"F16.wireOp",EDGE,"E55")])]})]});}
            var Q53;
            {var subQ0=sQuery(id+"F9.wireOp",EDGE,"E34");var subQ1=sQuery(id+"F11.wireOp",EDGE,"E37");var subQ2=sQuery(id+"F0.wireOp",EDGE,"E0");var subQ3=sQuery(id+"F0.wireOp",EDGE,"E1");var subQ4=sQuery(id+"F0.wireOp",EDGE,"E2");var subQ5=sQuery(id+"F0.wireOp",EDGE,"E3");Q53=makeQuery(id+"F19.boolean.opBoolean","MERGE",EDGE,{"derivedFrom":[makeQuery(id+"F15.boolean.opBoolean","SPLIT",EDGE,{"disambiguationData":[TD([makeQuery(id+"F15.opExtrude","SWEPT_FACE",FACE,{"disambiguationData":[OSD([sQuery(id+"F14.wireOp",EDGE,"E43.rect.bottom")])]})])],"derivedFrom":makeQuery(id+"F12.boolean.opBoolean","COPY",EDGE,{"derivedFrom":makeQuery(id+"F12.opExtrude","SWEPT_EDGE",EDGE,{"disambiguationData":[OSD([subQ0,subQ1,sQuery(id+"F11.wireOp",EDGE,"E42")])]})})}),makeQuery(id+"F19.opExtrude","SWEPT_EDGE",EDGE,{"disambiguationData":[OSD([subQ2,subQ3,subQ4,subQ5,subQ1,sQuery(id+"F18.wireOp",EDGE,"E61.0"),sQuery(id+"F18.wireOp",EDGE,"E62.0")])]})]});}
            var Q54;
            Q54=makeQuery(id+"F21.boolean.opBoolean","COPY",EDGE,{"derivedFrom":makeQuery(id+"F21.opExtrude","CAP_EDGE",EDGE,{"disambiguationData":[OSD([sQuery(id+"F20.wireOp",EDGE,"E64.rect.top")])],"isStart":true})});
            var Q55;
            Q55=makeQuery(id+"F21.boolean.opBoolean","COPY",EDGE,{"derivedFrom":makeQuery(id+"F21.opExtrude","CAP_EDGE",EDGE,{"disambiguationData":[OSD([sQuery(id+"F20.wireOp",EDGE,"E64.rect.right")])],"isStart":true})});
            var Q56;
            Q56=makeQuery(id+"F21.boolean.opBoolean","COPY",EDGE,{"derivedFrom":makeQuery(id+"F21.opExtrude","CAP_EDGE",EDGE,{"disambiguationData":[OSD([sQuery(id+"F20.wireOp",EDGE,"E64.rect.left")])],"isStart":true})});
            var Q57;
            Q57=makeQuery(id+"F21.boolean.opBoolean","COPY",EDGE,{"derivedFrom":makeQuery(id+"F21.opExtrude","CAP_EDGE",EDGE,{"disambiguationData":[OSD([sQuery(id+"F20.wireOp",EDGE,"E64.rect.bottom")])],"isStart":true})});
            var Q58;
            Q58=makeQuery(id+"F25.boolean.opBoolean","INTERSECT",EDGE,{"derivedFrom":[makeQuery(id+"F8.boolean.opBoolean","COPY",FACE,{"disambiguationData":[OD(1.0)],"derivedFrom":makeQuery(id+"F8.opExtrude","SWEPT_FACE",FACE,{"disambiguationData":[OSD([sQuery(id+"F7.wireOp",EDGE,"E28")])]})}),makeQuery(id+"F25.opExtrude","SWEPT_FACE",FACE,{"disambiguationData":[OSD([sQuery(id+"F24.wireOp",EDGE,"E72")])]})]});
            var Q59;
            Q59=makeQuery(id+"F25.boolean.opBoolean","INTERSECT",EDGE,{"derivedFrom":[makeQuery(id+"F8.boolean.opBoolean","COPY",FACE,{"disambiguationData":[OD(0.0)],"derivedFrom":makeQuery(id+"F8.opExtrude","SWEPT_FACE",FACE,{"disambiguationData":[OSD([sQuery(id+"F7.wireOp",EDGE,"E28")])]})}),makeQuery(id+"F25.opExtrude","SWEPT_FACE",FACE,{"disambiguationData":[OSD([sQuery(id+"F24.wireOp",EDGE,"E71")])]})]});
            var Q60;
            Q60=makeQuery(id+"F25.boolean.opBoolean","INTERSECT",EDGE,{"derivedFrom":[makeQuery(id+"F23.boolean.opBoolean","COPY",FACE,{"derivedFrom":makeQuery(id+"F23.opExtrude","SWEPT_FACE",FACE,{"disambiguationData":[OSD([sQuery(id+"F22.wireOp",EDGE,"E65.0.1")])]})}),makeQuery(id+"F25.opExtrude","SWEPT_FACE",FACE,{"disambiguationData":[OSD([sQuery(id+"F24.wireOp",EDGE,"E71")])]})]});
            var Q61;
            Q61=makeQuery(id+"F25.boolean.opBoolean","INTERSECT",EDGE,{"derivedFrom":[makeQuery(id+"F23.boolean.opBoolean","COPY",FACE,{"derivedFrom":makeQuery(id+"F23.opExtrude","SWEPT_FACE",FACE,{"disambiguationData":[OSD([sQuery(id+"F22.wireOp",EDGE,"E65.0.3")])]})}),makeQuery(id+"F25.opExtrude","SWEPT_FACE",FACE,{"disambiguationData":[OSD([sQuery(id+"F24.wireOp",EDGE,"E71")])]})]});
            var Q62;
            Q62=makeQuery(id+"F25.boolean.opBoolean","INTERSECT",EDGE,{"derivedFrom":[makeQuery(id+"F21.boolean.opBoolean","COPY",FACE,{"derivedFrom":makeQuery(id+"F21.opExtrude","SWEPT_FACE",FACE,{"disambiguationData":[OSD([sQuery(id+"F20.wireOp",EDGE,"E64.rect.top")])]})}),makeQuery(id+"F25.opExtrude","SWEPT_FACE",FACE,{"disambiguationData":[OSD([sQuery(id+"F24.wireOp",EDGE,"E72")])]})]});
            var Q63;
            Q63=makeQuery(id+"F25.boolean.opBoolean","INTERSECT",EDGE,{"derivedFrom":[makeQuery(id+"F21.boolean.opBoolean","COPY",FACE,{"derivedFrom":makeQuery(id+"F21.opExtrude","SWEPT_FACE",FACE,{"disambiguationData":[OSD([sQuery(id+"F20.wireOp",EDGE,"E64.rect.bottom")])]})}),makeQuery(id+"F25.opExtrude","SWEPT_FACE",FACE,{"disambiguationData":[OSD([sQuery(id+"F24.wireOp",EDGE,"E72")])]})]});
            var Q64;
            Q64=makeQuery(id+"F30.boolean.opBoolean","INTERSECT",EDGE,{"derivedFrom":[makeQuery(id+"F4.opExtrude","CAP_FACE",FACE,{"disambiguationData":[OSD([dummyQuery(id+"F2.planeOp",FACE)])],"isStart":false}),makeQuery(id+"F30.opExtrude","SWEPT_FACE",FACE,{"disambiguationData":[OSD([sQuery(id+"F29.wireOp",EDGE,"E78")])]})]});
            var Q65;
            Q65=makeQuery(id+"F30.boolean.opBoolean","INTERSECT",EDGE,{"derivedFrom":[makeQuery(id+"F4.opExtrude","CAP_FACE",FACE,{"disambiguationData":[OSD([dummyQuery(id+"F2.planeOp",FACE)])],"isStart":false}),makeQuery(id+"F30.opExtrude","SWEPT_FACE",FACE,{"disambiguationData":[OSD([sQuery(id+"F29.wireOp",EDGE,"E79")])]})]});
            var Q66;
            Q66=makeQuery(id+"F34.boolean.opBoolean","COPY",EDGE,{"derivedFrom":makeQuery(id+"F34.opExtrude","CAP_EDGE",EDGE,{"disambiguationData":[OSD([sQuery(id+"F33.wireOp",EDGE,"E86")])],"isStart":true})});
            var Q67;
            Q67=makeQuery(id+"F34.boolean.opBoolean","COPY",EDGE,{"derivedFrom":makeQuery(id+"F34.opExtrude","TWEAK_EDGE",EDGE,{"derivedFrom":[makeQuery(id+"F4.opExtrude","SWEPT_FACE",FACE,{"disambiguationData":[OSD([sQuery(id+"F3.wireOp",EDGE,"E10")])]}),makeQuery(id+"F33.imprint","IMPRINT",EDGE,{"derivedFrom":sQuery(id+"F33.wireOp",EDGE,"E86")})]})});
            var Q68;
            Q68=makeQuery(id+"F36.opExtrude","CAP_EDGE",EDGE,{"disambiguationData":[OSD([sQuery(id+"F35.wireOp",EDGE,"E90.0")])],"isStart":true});
            var Q69;
            Q69=makeQuery(id+"F36.opExtrude","CAP_EDGE",EDGE,{"disambiguationData":[OSD([sQuery(id+"F35.wireOp",EDGE,"E88.0")])],"isStart":true});
            var Q70;
            Q70=makeQuery(id+"F36.opExtrude","CAP_EDGE",EDGE,{"disambiguationData":[OSD([sQuery(id+"F35.wireOp",EDGE,"E89.0")])],"isStart":true});
            var Q71;
            Q71=makeQuery(id+"F36.opExtrude","CAP_EDGE",EDGE,{"disambiguationData":[OSD([sQuery(id+"F35.wireOp",EDGE,"E93")])],"isStart":true});
            var Q72;
            Q72=makeQuery(id+"F36.opExtrude","CAP_EDGE",EDGE,{"disambiguationData":[OSD([sQuery(id+"F35.wireOp",EDGE,"E94")])],"isStart":true});
            var Q73;
            Q73=makeQuery(id+"F36.opExtrude","CAP_EDGE",EDGE,{"disambiguationData":[OSD([sQuery(id+"F35.wireOp",EDGE,"E87.0")])],"isStart":true});
            var Q74;
            Q74=makeQuery(id+"F36.opExtrude","SWEPT_EDGE",EDGE,{"disambiguationData":[OSD([sQuery(id+"F35.wireOp",EDGE,"E87.0"),sQuery(id+"F35.wireOp",EDGE,"E88.0")])]});
            var Q75;
            Q75=makeQuery(id+"F36.opExtrude","CAP_EDGE",EDGE,{"disambiguationData":[OSD([sQuery(id+"F35.wireOp",EDGE,"E87.0")])],"isStart":false});
            var Q76;
            Q76=makeQuery(id+"F36.opExtrude","SWEPT_EDGE",EDGE,{"disambiguationData":[OSD([sQuery(id+"F35.wireOp",EDGE,"E87.0"),sQuery(id+"F35.wireOp",EDGE,"E94")])]});
            var Q77;
            Q77=makeQuery(id+"F42.boolean.opBoolean","COPY",EDGE,{"derivedFrom":makeQuery(id+"F42.opExtrude","CAP_EDGE",EDGE,{"disambiguationData":[OSD([sQuery(id+"F41.wireOp",EDGE,"E106")])],"isStart":true})});
            var Q78;
            Q78=makeQuery(id+"F42.boolean.opBoolean","INTERSECT",EDGE,{"derivedFrom":[makeQuery(id+"F36.opExtrude","SWEPT_FACE",FACE,{"disambiguationData":[OSD([sQuery(id+"F35.wireOp",EDGE,"E94")])]}),makeQuery(id+"F42.opExtrude","SWEPT_FACE",FACE,{"disambiguationData":[OSD([sQuery(id+"F41.wireOp",EDGE,"E106")])]})]});
            var Q79;
            Q79=makeQuery(id+"F36.opExtrude","SWEPT_EDGE",EDGE,{"disambiguationData":[OSD([sQuery(id+"F35.wireOp",EDGE,"E90.0"),sQuery(id+"F35.wireOp",EDGE,"E91.0")])]});
            var Q80;
            Q80=makeQuery(id+"F36.opExtrude","CAP_EDGE",EDGE,{"disambiguationData":[OSD([sQuery(id+"F35.wireOp",EDGE,"E91.0")])],"isStart":true});
            var Q81;
            Q81=makeQuery(id+"F36.opExtrude","CAP_EDGE",EDGE,{"disambiguationData":[OSD([sQuery(id+"F35.wireOp",EDGE,"E92.0")])],"isStart":true});
            var Q82;
            Q82=makeQuery(id+"F36.opExtrude","SWEPT_EDGE",EDGE,{"disambiguationData":[OSD([sQuery(id+"F35.wireOp",EDGE,"E91.0"),sQuery(id+"F35.wireOp",EDGE,"E92.0")])]});
            var Q83;
            Q83=makeQuery(id+"F36.opExtrude","CAP_EDGE",EDGE,{"disambiguationData":[OSD([sQuery(id+"F35.wireOp",EDGE,"E91.0")])],"isStart":false});
            var Q84;
            Q84=makeQuery(id+"F36.opExtrude","CAP_EDGE",EDGE,{"disambiguationData":[OSD([sQuery(id+"F35.wireOp",EDGE,"E88.0")])],"isStart":false});
            var Q85;
            Q85=makeQuery(id+"F36.opExtrude","CAP_EDGE",EDGE,{"disambiguationData":[OSD([sQuery(id+"F35.wireOp",EDGE,"E94")])],"isStart":false});
            var Q86;
            Q86=makeQuery(id+"F36.opExtrude","CAP_EDGE",EDGE,{"disambiguationData":[OSD([sQuery(id+"F35.wireOp",EDGE,"E89.0")])],"isStart":false});
            var Q87;
            Q87=makeQuery(id+"F36.opExtrude","CAP_EDGE",EDGE,{"disambiguationData":[OSD([sQuery(id+"F35.wireOp",EDGE,"E90.0")])],"isStart":false});
            var Q88;
            Q88=makeQuery(id+"F36.opExtrude","CAP_EDGE",EDGE,{"disambiguationData":[OSD([sQuery(id+"F35.wireOp",EDGE,"E92.0")])],"isStart":false});
            var Q89;
            Q89=makeQuery(id+"F36.opExtrude","SWEPT_EDGE",EDGE,{"disambiguationData":[OSD([sQuery(id+"F35.wireOp",EDGE,"E92.0"),sQuery(id+"F35.wireOp",EDGE,"E93")])]});
            var Q90;
            Q90=makeQuery(id+"F36.opExtrude","CAP_EDGE",EDGE,{"disambiguationData":[OSD([sQuery(id+"F35.wireOp",EDGE,"E93")])],"isStart":false});
            var Q91;
            Q91=makeQuery(id+"F36.opExtrude","SWEPT_EDGE",EDGE,{"disambiguationData":[OSD([sQuery(id+"F35.wireOp",EDGE,"E93"),sQuery(id+"F35.wireOp",EDGE,"E94")])]});
            var Q92;
            Q92=makeQuery(id+"F38.boolean.opBoolean","COPY",EDGE,{"derivedFrom":makeQuery(id+"F38.opExtrude","CAP_EDGE",EDGE,{"disambiguationData":[OSD([sQuery(id+"F37.wireOp",EDGE,"E96.0")])],"isStart":true})});
            var Q93;
            Q93=makeQuery(id+"F38.boolean.opBoolean","COPY",EDGE,{"derivedFrom":makeQuery(id+"F38.opExtrude","CAP_EDGE",EDGE,{"disambiguationData":[OSD([sQuery(id+"F37.wireOp",EDGE,"E95.0")])],"isStart":true})});
            var Q94;
            Q94=makeQuery(id+"F38.boolean.opBoolean","INTERSECT",EDGE,{"derivedFrom":[makeQuery(id+"F36.opExtrude","CAP_FACE",FACE,{"disambiguationData":[OSD([sQuery(id+"F35.wireOp",EDGE,"E87.0"),sQuery(id+"F35.wireOp",EDGE,"E88.0"),sQuery(id+"F35.wireOp",EDGE,"E89.0"),sQuery(id+"F35.wireOp",EDGE,"E90.0"),sQuery(id+"F35.wireOp",EDGE,"E91.0"),sQuery(id+"F35.wireOp",EDGE,"E92.0"),sQuery(id+"F35.wireOp",EDGE,"E93"),sQuery(id+"F35.wireOp",EDGE,"E94")])],"isStart":false}),makeQuery(id+"F38.opExtrude","SWEPT_FACE",FACE,{"disambiguationData":[OSD([sQuery(id+"F37.wireOp",EDGE,"E95.0")])]})]});
            var Q95;
            Q95=makeQuery(id+"F38.boolean.opBoolean","INTERSECT",EDGE,{"derivedFrom":[makeQuery(id+"F36.opExtrude","CAP_FACE",FACE,{"disambiguationData":[OSD([sQuery(id+"F35.wireOp",EDGE,"E87.0"),sQuery(id+"F35.wireOp",EDGE,"E88.0"),sQuery(id+"F35.wireOp",EDGE,"E89.0"),sQuery(id+"F35.wireOp",EDGE,"E90.0"),sQuery(id+"F35.wireOp",EDGE,"E91.0"),sQuery(id+"F35.wireOp",EDGE,"E92.0"),sQuery(id+"F35.wireOp",EDGE,"E93"),sQuery(id+"F35.wireOp",EDGE,"E94")])],"isStart":false}),makeQuery(id+"F38.opExtrude","SWEPT_FACE",FACE,{"disambiguationData":[OSD([sQuery(id+"F37.wireOp",EDGE,"E96.0")])]})]});
            var Q96;
            {var subQ0=sQuery(id+"F9.wireOp",EDGE,"E34");var subQ1=sQuery(id+"F11.wireOp",EDGE,"E39");var subQ2=sQuery(id+"F0.wireOp",EDGE,"E0");var subQ3=sQuery(id+"F0.wireOp",EDGE,"E1");var subQ4=sQuery(id+"F0.wireOp",EDGE,"E2");var subQ5=sQuery(id+"F0.wireOp",EDGE,"E3");Q96=makeQuery(id+"F19.boolean.opBoolean","MERGE",EDGE,{"derivedFrom":[makeQuery(id+"F15.boolean.opBoolean","SPLIT",EDGE,{"disambiguationData":[TD([makeQuery(id+"F15.opExtrude","SWEPT_FACE",FACE,{"disambiguationData":[OSD([sQuery(id+"F14.wireOp",EDGE,"E43.rect.bottom")])]})])],"derivedFrom":makeQuery(id+"F12.boolean.opBoolean","COPY",EDGE,{"derivedFrom":makeQuery(id+"F12.opExtrude","SWEPT_EDGE",EDGE,{"disambiguationData":[OSD([subQ0,subQ1,sQuery(id+"F11.wireOp",EDGE,"E42")])]})})}),makeQuery(id+"F19.opExtrude","SWEPT_EDGE",EDGE,{"disambiguationData":[OSD([subQ2,subQ3,subQ4,subQ5,subQ1,sQuery(id+"F18.wireOp",EDGE,"E60.0"),sQuery(id+"F18.wireOp",EDGE,"E62.0")])]})]});}
            var Q97;
            Q97=makeQuery(id+"F4.opExtrude","TWEAK_EDGE",EDGE,{"derivedFrom":[dummyQuery(id+"F2.planeOp",FACE),makeQuery(id+"F3.imprint","IMPRINT",EDGE,{"derivedFrom":sQuery(id+"F3.wireOp",EDGE,"E15.0")})]});
            fillet(context, id + "F43", {"entities" : qUnion([Q0, Q1, Q2, Q3, Q4, Q5, Q6, Q7, Q8, Q9, Q10, Q11, Q12, Q13, Q14, Q15, Q16, Q17, Q18, Q19, Q20, Q21, Q22, Q23, Q24, Q25, Q26, Q27, Q28, Q29, Q30, Q31, Q32, Q33, Q34, Q35, Q36, Q37, Q38, Q39, Q40, Q41, Q42, Q43, Q44, Q45, Q46, Q47, Q48, Q49, Q50, Q51, Q52, Q53, Q54, Q55, Q56, Q57, Q58, Q59, Q60, Q61, Q62, Q63, Q64, Q65, Q66, Q67, Q68, Q69, Q70, Q71, Q72, Q73, Q74, Q75, Q76, Q77, Q78, Q79, Q80, Q81, Q82, Q83, Q84, Q85, Q86, Q87, Q88, Q89, Q90, Q91, Q92, Q93, Q94, Q95, Q96, Q97]), "radius" : .5 * mm, "tangentPropagation" : true, "allowEdgeOverflow" : false});
        }
        {
            var Q0;
            {var subQ0=sQuery(id+"F3.wireOp",EDGE,"E16");var subQ1=sQuery(id+"F3.wireOp",EDGE,"E10");var subQ2=sQuery(id+"F3.wireOp",EDGE,"E8");var subQ3=sQuery(id+"F3.wireOp",EDGE,"E7");var subQ4=sQuery(id+"F3.wireOp",EDGE,"E9");var subQ5=sQuery(id+"F0.wireOp",EDGE,"E0");var subQ6=sQuery(id+"F3.wireOp",EDGE,"E5");var subQ7=sQuery(id+"F3.wireOp",EDGE,"E14");var subQ8=sQuery(id+"F0.wireOp",EDGE,"E1");var subQ9=sQuery(id+"F3.wireOp",EDGE,"E6");Q0=makeQuery(id+"F17.boolean.opBoolean","MERGE",FACE,{"derivedFrom":[makeQuery(id+"F8.boolean.opBoolean","SPLIT",FACE,{"disambiguationData":[TD([makeQuery(id+"F1.opExtrude","SWEPT_FACE",FACE,{"disambiguationData":[OSD([subQ5])]})])],"derivedFrom":makeQuery(id+"F4.boolean.opBoolean","MERGE",FACE,{"derivedFrom":[makeQuery(id+"F1.opExtrude","CAP_FACE",FACE,{"disambiguationData":[OSD([subQ5,subQ8,sQuery(id+"F0.wireOp",EDGE,"E2"),sQuery(id+"F0.wireOp",EDGE,"E3")])],"isStart":true}),makeQuery(id+"F4.opExtrude","CAP_FACE",FACE,{"disambiguationData":[OSD([subQ6,subQ9,subQ3,subQ2,subQ4,subQ1,sQuery(id+"F3.wireOp",EDGE,"E11"),subQ7,sQuery(id+"F3.wireOp",EDGE,"E15.0"),subQ0])],"isStart":true})]})}),makeQuery(id+"F17.opExtrude","CAP_FACE",FACE,{"disambiguationData":[OSD([sQuery(id+"F16.wireOp",EDGE,"E49"),sQuery(id+"F16.wireOp",EDGE,"E50.0"),sQuery(id+"F16.wireOp",EDGE,"E55"),sQuery(id+"F16.wireOp",EDGE,"E56")])],"isStart":true})]});}
            var sketch = newSketch(context, id + "F44", { "sketchPlane" : qUnion([Q0])});
            skCircle(sketch, "E107.cCircle", {"center": v(-23.1, 16) * mm, "radius": 2.85 * mm, "construction": true});
            skLineSegment(sketch, "E107.0", {"start": v(-24.75, 18.85) * mm, "end": v(-21.45, 18.85) * mm});
            skLineSegment(sketch, "E107.1", {"start": v(-21.45, 18.85) * mm, "end": v(-19.8, 16) * mm});
            skLineSegment(sketch, "E107.2", {"start": v(-19.8, 16) * mm, "end": v(-21.45, 13.15) * mm});
            skLineSegment(sketch, "E107.3", {"start": v(-21.45, 13.15) * mm, "end": v(-24.75, 13.15) * mm});
            skLineSegment(sketch, "E107.4", {"start": v(-24.75, 13.15) * mm, "end": v(-26.4, 16) * mm});
            skLineSegment(sketch, "E107.5", {"start": v(-26.4, 16) * mm, "end": v(-24.75, 18.85) * mm});
            skPoint(sketch, "E107.0.midPoint", {"position": v(-23.1, 18.85) * mm});
            skCircle(sketch, "E108.cCircle", {"center": v(-23.1, 4) * mm, "radius": 2.85 * mm, "construction": true});
            skLineSegment(sketch, "E108.0", {"start": v(-21.45, 1.15) * mm, "end": v(-24.75, 1.15) * mm});
            skLineSegment(sketch, "E108.1", {"start": v(-24.75, 1.15) * mm, "end": v(-26.4, 4) * mm});
            skLineSegment(sketch, "E108.2", {"start": v(-26.4, 4) * mm, "end": v(-24.75, 6.85) * mm});
            skLineSegment(sketch, "E108.3", {"start": v(-24.75, 6.85) * mm, "end": v(-21.45, 6.85) * mm});
            skLineSegment(sketch, "E108.4", {"start": v(-21.45, 6.85) * mm, "end": v(-19.8, 4) * mm});
            skLineSegment(sketch, "E108.5", {"start": v(-19.8, 4) * mm, "end": v(-21.45, 1.15) * mm});
            skPoint(sketch, "E108.0.midPoint", {"position": v(-23.1, 1.15) * mm});
            skSolve(sketch);
        }
        {
            var Q0;
            Q0 = qSketchRegion(id + "F44", true);
            extrude(context, id + "F45", {"entities" : qUnion([Q0]), "operationType" : NewBodyOperationType.REMOVE, "oppositeDirection" : true, "depth" : 3 * mm, "offsetDistance" : 25 * mm});
        }
        {
            var Q0;
            Q0=makeQuery(id+"F45.boolean.opBoolean","INTERSECT",EDGE,{"derivedFrom":[makeQuery(id+"F30.boolean.opBoolean","COPY",FACE,{"derivedFrom":makeQuery(id+"F30.opExtrude","SWEPT_FACE",FACE,{"disambiguationData":[OSD([sQuery(id+"F29.wireOp",EDGE,"E78")])]})}),makeQuery(id+"F45.opExtrude","CAP_FACE",FACE,{"disambiguationData":[OSD([sQuery(id+"F44.wireOp",EDGE,"E107.0"),sQuery(id+"F44.wireOp",EDGE,"E107.1"),sQuery(id+"F44.wireOp",EDGE,"E107.2"),sQuery(id+"F44.wireOp",EDGE,"E107.3"),sQuery(id+"F44.wireOp",EDGE,"E107.4"),sQuery(id+"F44.wireOp",EDGE,"E107.5")])],"isStart":false})]});
            var Q1;
            Q1=makeQuery(id+"F45.boolean.opBoolean","INTERSECT",EDGE,{"derivedFrom":[makeQuery(id+"F30.boolean.opBoolean","COPY",FACE,{"derivedFrom":makeQuery(id+"F30.opExtrude","SWEPT_FACE",FACE,{"disambiguationData":[OSD([sQuery(id+"F29.wireOp",EDGE,"E79")])]})}),makeQuery(id+"F45.opExtrude","CAP_FACE",FACE,{"disambiguationData":[OSD([sQuery(id+"F44.wireOp",EDGE,"E108.0"),sQuery(id+"F44.wireOp",EDGE,"E108.1"),sQuery(id+"F44.wireOp",EDGE,"E108.2"),sQuery(id+"F44.wireOp",EDGE,"E108.3"),sQuery(id+"F44.wireOp",EDGE,"E108.4"),sQuery(id+"F44.wireOp",EDGE,"E108.5")])],"isStart":false})]});
            chamfer(context, id + "F46", {"entities" : qUnion([Q0, Q1]), "width" : 1.2 * mm, "tangentPropagation" : true});
        }
        {
            var Q0;
            Q0=qCreatedBy(id+"F2.planeOp",FACE);
            var sketch = newSketch(context, id + "F47", { "sketchPlane" : qUnion([Q0])});
            skCircle(sketch, "E109", {"center": v(0, 0) * mm, "radius": 9.75 * mm});
            skCircle(sketch, "E110", {"center": v(0, 0) * mm, "radius": 8.25 * mm});
            skCircle(sketch, "E111", {"center": v(0, 0) * mm, "radius": 9 * mm, "construction": true});
            skLineSegment(sketch, "E112", {"start": v(0, 0) * mm, "end": v(8.25, 0) * mm, "construction": true});
            skLineSegment(sketch, "E113", {"start": v(8.25, 0) * mm, "end": v(9, 0) * mm, "construction": true});
            skLineSegment(sketch, "E114", {"start": v(9, 0) * mm, "end": v(9.75, 0) * mm, "construction": true});
            skSolve(sketch);
        }
        {
            var Q0;
            Q0=qSketchRegion(id+"F47",true);
            extrude(context, id + "F48", {"entities" : qUnion([Q0]), "operationType" : NewBodyOperationType.REMOVE, "oppositeDirection" : true, "depth" : 3.5 * mm, "symmetric" : true});
        }
        {
            var Q0;
            Q0=makeQuery(id+"F48.boolean.opBoolean","INTERSECT",EDGE,{"derivedFrom":[makeQuery(id+"F12.boolean.opBoolean","COPY",FACE,{"derivedFrom":makeQuery(id+"F12.opExtrude","SWEPT_FACE",FACE,{"disambiguationData":[OSD([sQuery(id+"F11.wireOp",EDGE,"E37")])]})}),makeQuery(id+"F48.opExtrude","SWEPT_FACE",FACE,{"disambiguationData":[OSD([sQuery(id+"F47.wireOp",EDGE,"E109")])]})]});
            var Q1;
            Q1=makeQuery(id+"F48.boolean.opBoolean","INTERSECT",EDGE,{"derivedFrom":[makeQuery(id+"F12.boolean.opBoolean","COPY",FACE,{"derivedFrom":makeQuery(id+"F12.opExtrude","SWEPT_FACE",FACE,{"disambiguationData":[OSD([sQuery(id+"F11.wireOp",EDGE,"E39")])]})}),makeQuery(id+"F48.opExtrude","SWEPT_FACE",FACE,{"disambiguationData":[OSD([sQuery(id+"F47.wireOp",EDGE,"E109")])]})]});
            var Q2;
            Q2=makeQuery(id+"F48.boolean.opBoolean","INTERSECT",EDGE,{"derivedFrom":[makeQuery(id+"F15.boolean.opBoolean","COPY",FACE,{"derivedFrom":makeQuery(id+"F15.opExtrude","SWEPT_FACE",FACE,{"disambiguationData":[OSD([sQuery(id+"F14.wireOp",EDGE,"E43.rect.left")])]})}),makeQuery(id+"F48.opExtrude","SWEPT_FACE",FACE,{"disambiguationData":[OSD([sQuery(id+"F47.wireOp",EDGE,"E110")])]})]});
            var Q3;
            Q3=makeQuery(id+"F48.boolean.opBoolean","INTERSECT",EDGE,{"derivedFrom":[makeQuery(id+"F15.boolean.opBoolean","COPY",FACE,{"derivedFrom":makeQuery(id+"F15.opExtrude","SWEPT_FACE",FACE,{"disambiguationData":[OSD([sQuery(id+"F14.wireOp",EDGE,"E43.rect.right")])]})}),makeQuery(id+"F48.opExtrude","SWEPT_FACE",FACE,{"disambiguationData":[OSD([sQuery(id+"F47.wireOp",EDGE,"E110")])]})]});
            fillet(context, id + "F49", {"entities" : qUnion([Q0, Q1, Q2, Q3]), "radius" : .5 * mm, "tangentPropagation" : true, "allowEdgeOverflow" : false});
        }
        {
            var Q0;
            Q0=qCreatedBy(makeId("Front.planeOp"),FACE);
            cPlane(context, id + "F50", {"entities" : qUnion([Q0]), "cplaneType" : CPlaneType.OFFSET, "offset" : 20 * mm, "oppositeDirection" : true, "width" : 150 * mm, "height" : 150 * mm});
        }
        {
            var Q0;
            Q0=makeQuery(id+"F8.boolean.opBoolean","SPLIT",BODY,{"disambiguationData":[OD(1.0)],"derivedFrom":makeQuery(id+"F1.opExtrude","SWEPT_BODY",BODY,{"disambiguationData":[OSD([sQuery(id+"F0.wireOp",EDGE,"E0"),sQuery(id+"F0.wireOp",EDGE,"E1"),sQuery(id+"F0.wireOp",EDGE,"E2"),sQuery(id+"F0.wireOp",EDGE,"E3")])]})});
            var Q1;
            Q1=makeQuery(id+"F8.boolean.opBoolean","SPLIT",BODY,{"disambiguationData":[OD(0.0)],"derivedFrom":makeQuery(id+"F1.opExtrude","SWEPT_BODY",BODY,{"disambiguationData":[OSD([sQuery(id+"F0.wireOp",EDGE,"E0"),sQuery(id+"F0.wireOp",EDGE,"E1"),sQuery(id+"F0.wireOp",EDGE,"E2"),sQuery(id+"F0.wireOp",EDGE,"E3")])]})});
            var Q2;
            Q2=qCreatedBy(id+"F50.planeOp",FACE);
            mirror(context, id + "F51", {"entities" : qUnion([Q0, Q1]), "mirrorPlane" : qUnion([Q2])});
        }
        {
            var Q0;
            {var subQ0=sQuery(id+"F0.wireOp",EDGE,"E1");var subQ3=sQuery(id+"F0.wireOp",EDGE,"E3");Q0=makeQuery(id+"F8.boolean.opBoolean","SPLIT",FACE,{"disambiguationData":[TD([makeQuery(id+"F1.opExtrude","SWEPT_FACE",FACE,{"disambiguationData":[OSD([subQ3])]})])],"derivedFrom":makeQuery(id+"F1.opExtrude","SWEPT_FACE",FACE,{"disambiguationData":[OSD([subQ0])]})});}
            var sketch = newSketch(context, id + "F52", { "sketchPlane" : qUnion([Q0])});
            skLineSegment(sketch, "E115", {"start": v(-30.01, 20) * mm, "end": v(-33.5, 20) * mm, "construction": true});
            skLineSegment(sketch, "E116", {"start": v(-25.01, 20) * mm, "end": v(-21.53, 20) * mm, "construction": true});
            skArc(sketch, "E117.0", {"start": v(58, 15.59) * mm, "mid": v(61.53, 20) * mm, "end": v(58, 24.41) * mm, "construction": true});
            skLineSegment(sketch, "E118", {"start": v(-17, 20) * mm, "end": v(20, 20) * mm, "construction": true});
            skLineSegment(sketch, "E119", {"start": v(20, 20) * mm, "end": v(57, 20) * mm, "construction": true});
            skLineSegment(sketch, "E120", {"start": v(57, 20) * mm, "end": v(61.53, 20) * mm, "construction": true});
            skLineSegment(sketch, "E121", {"start": v(61.53, 20) * mm, "end": v(65.01, 20) * mm, "construction": true});
            skText(sketch, "E122", { "text": "Eustathios", "fontName": "OpenSans-BoldItalic.ttf"});
            skLineSegment(sketch, "E123", {"start": v(70.01, 20) * mm, "end": v(73.5, 20) * mm, "construction": true});
            skText(sketch, "E124", { "text": "Eustathios", "fontName": "OpenSans-BoldItalic.ttf"});
            const initialGuessF52  = {"E122": [0.07001, 0.00273, 0, 1, 0.005], "E124": [-0.02501, 0.00273, 0, 1, 0.005]};
            skSetInitialGuess(sketch, initialGuessF52);
            skSolve(sketch);
        }
        {
            var Q0;
            Q0=qSketchRegion(id+"F52",true);
            extrude(context, id + "F53", {"entities" : qUnion([Q0]), "operationType" : NewBodyOperationType.REMOVE, "oppositeDirection" : true, "depth" : .5 * mm});
        }
    });
